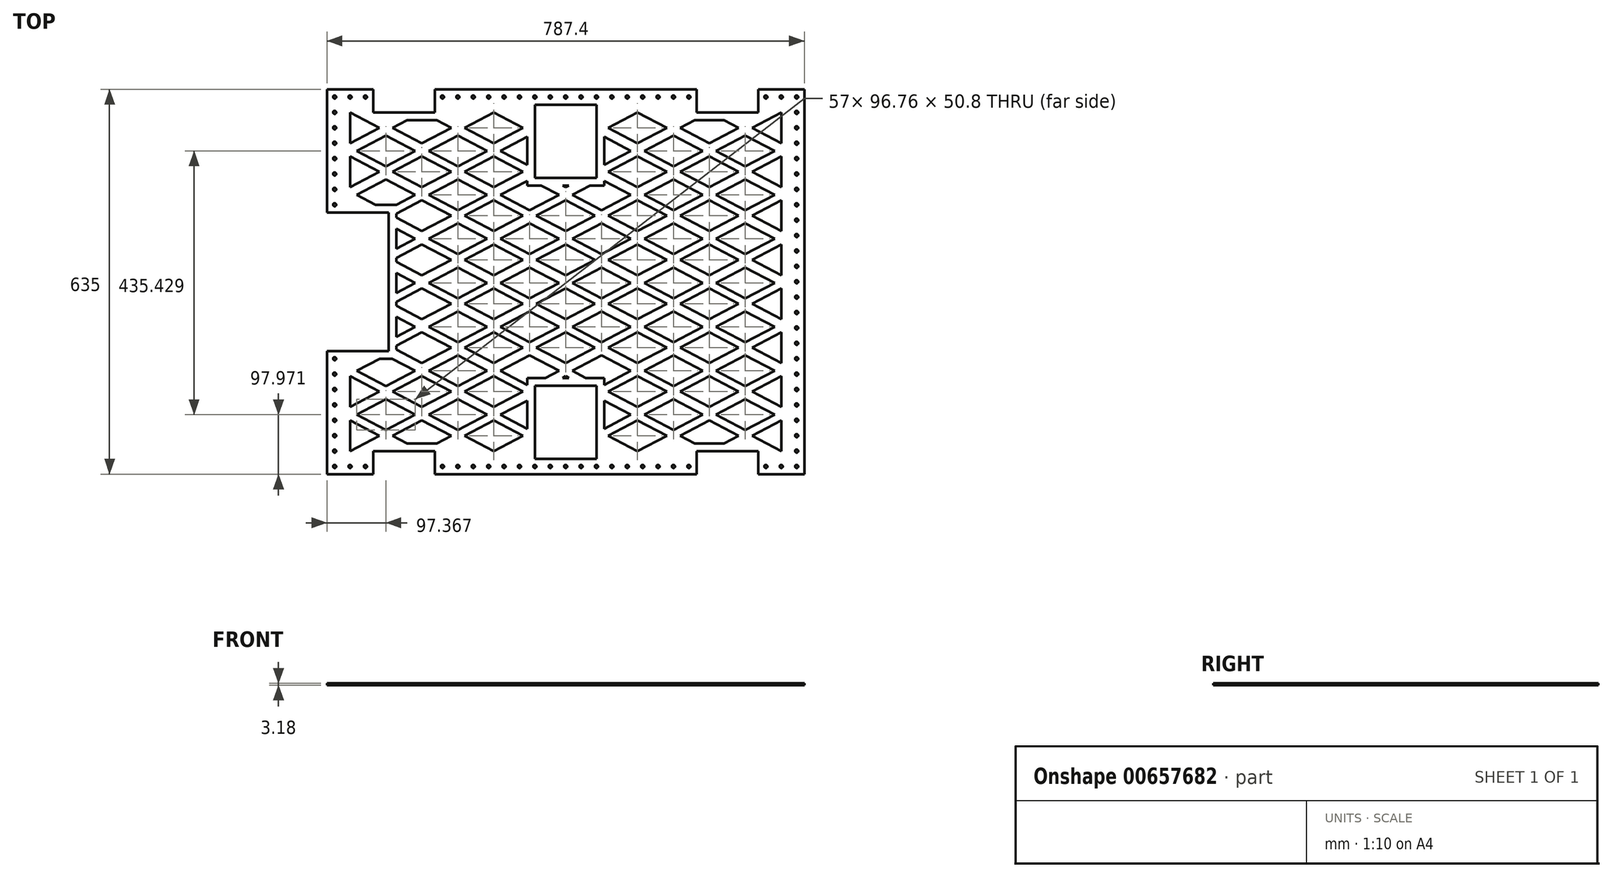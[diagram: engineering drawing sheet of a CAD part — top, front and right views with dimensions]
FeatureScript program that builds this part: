
annotation { "Feature Type Name" : "Feature", "Feature Type Description" : "" }
export const myFeature = defineFeature(function(context is Context, id is Id, definition is map)
    precondition{}
    {
        {
            var Q0;
            Q0=qCreatedBy(makeId("Top.planeOp"),FACE);
            var sketch = newSketch(context, id + "F0", { "sketchPlane" : qUnion([Q0])});
            skLineSegment(sketch, "E0.bottom", {"start": v(0, 0) * mm, "end": v(787.4, 0) * mm});
            skLineSegment(sketch, "E0.top", {"start": v(0, -635) * mm, "end": v(787.4, -635) * mm});
            skLineSegment(sketch, "E0.left", {"start": v(0, 0) * mm, "end": v(0, -635) * mm});
            skLineSegment(sketch, "E0.right", {"start": v(787.4, 0) * mm, "end": v(787.4, -635) * mm});
            skCircle(sketch, "E1", {"center": v(12.7, -622.3) * mm, "radius": 2.55 * mm});
            skCircle(sketch, "E2.0.1.0", {"center": v(12.7, -596.9) * mm, "radius": 2.55 * mm});
            skLineSegment(sketch, "E2.direction1", {"start": v(12.7, -622.3) * mm, "end": v(38.1, -622.3) * mm, "construction": true});
            skLineSegment(sketch, "E2.direction2", {"start": v(12.7, -622.3) * mm, "end": v(12.7, -596.9) * mm, "construction": true});
            skCircle(sketch, "E3.0.0.2", {"center": v(12.7, -571.5) * mm, "radius": 2.55 * mm});
            skCircle(sketch, "E4.0.0.3", {"center": v(12.7, -546.1) * mm, "radius": 2.55 * mm});
            skCircle(sketch, "E5.0.0.4", {"center": v(12.7, -520.7) * mm, "radius": 2.55 * mm});
            skCircle(sketch, "E6.0.0.5", {"center": v(12.7, -495.3) * mm, "radius": 2.55 * mm});
            skCircle(sketch, "E7.0.0.6", {"center": v(12.7, -469.9) * mm, "radius": 2.55 * mm});
            skCircle(sketch, "E8.0.0.7", {"center": v(12.7, -444.5) * mm, "radius": 2.55 * mm});
            skCircle(sketch, "E9.0.0.8", {"center": v(12.7, -419.1) * mm, "radius": 2.55 * mm});
            skCircle(sketch, "E10.0.0.9", {"center": v(12.7, -393.7) * mm, "radius": 2.55 * mm});
            skCircle(sketch, "E11.0.0.10", {"center": v(12.7, -368.3) * mm, "radius": 2.55 * mm});
            skCircle(sketch, "E12.0.0.11", {"center": v(12.7, -342.9) * mm, "radius": 2.55 * mm});
            skCircle(sketch, "E13.0.0.12", {"center": v(12.7, -317.5) * mm, "radius": 2.55 * mm});
            skCircle(sketch, "E14.0.0.13", {"center": v(12.7, -292.1) * mm, "radius": 2.55 * mm});
            skCircle(sketch, "E15.0.0.14", {"center": v(12.7, -266.7) * mm, "radius": 2.55 * mm});
            skCircle(sketch, "E16.0.0.15", {"center": v(12.7, -241.3) * mm, "radius": 2.55 * mm});
            skCircle(sketch, "E17.0.0.16", {"center": v(12.7, -215.9) * mm, "radius": 2.55 * mm});
            skCircle(sketch, "E18.0.0.17", {"center": v(12.7, -190.5) * mm, "radius": 2.55 * mm});
            skCircle(sketch, "E19.0.0.18", {"center": v(12.7, -165.1) * mm, "radius": 2.55 * mm});
            skCircle(sketch, "E20.0.0.19", {"center": v(12.7, -139.7) * mm, "radius": 2.55 * mm});
            skCircle(sketch, "E21.0.0.20", {"center": v(12.7, -114.3) * mm, "radius": 2.55 * mm});
            skCircle(sketch, "E22.0.0.21", {"center": v(12.7, -88.9) * mm, "radius": 2.55 * mm});
            skCircle(sketch, "E23.0.0.22", {"center": v(12.7, -63.5) * mm, "radius": 2.55 * mm});
            skCircle(sketch, "E24.0.0.23", {"center": v(12.7, -38.1) * mm, "radius": 2.55 * mm});
            skCircle(sketch, "E25.0.0.24", {"center": v(12.7, -12.7) * mm, "radius": 2.55 * mm});
            skCircle(sketch, "E26.1.0.0", {"center": v(38.1, -622.3) * mm, "radius": 2.55 * mm});
            skCircle(sketch, "E26.2.0.0", {"center": v(63.5, -622.3) * mm, "radius": 2.55 * mm});
            skCircle(sketch, "E26.3.0.0", {"center": v(88.9, -622.3) * mm, "radius": 2.55 * mm});
            skCircle(sketch, "E26.4.0.0", {"center": v(114.3, -622.3) * mm, "radius": 2.55 * mm});
            skCircle(sketch, "E26.5.0.0", {"center": v(139.7, -622.3) * mm, "radius": 2.55 * mm});
            skCircle(sketch, "E26.6.0.0", {"center": v(165.1, -622.3) * mm, "radius": 2.55 * mm});
            skCircle(sketch, "E26.7.0.0", {"center": v(190.5, -622.3) * mm, "radius": 2.55 * mm});
            skCircle(sketch, "E26.8.0.0", {"center": v(215.9, -622.3) * mm, "radius": 2.55 * mm});
            skCircle(sketch, "E26.9.0.0", {"center": v(241.3, -622.3) * mm, "radius": 2.55 * mm});
            skCircle(sketch, "E26.10.0.0", {"center": v(266.7, -622.3) * mm, "radius": 2.55 * mm});
            skCircle(sketch, "E26.11.0.0", {"center": v(292.1, -622.3) * mm, "radius": 2.55 * mm});
            skCircle(sketch, "E26.12.0.0", {"center": v(317.5, -622.3) * mm, "radius": 2.55 * mm});
            skCircle(sketch, "E26.13.0.0", {"center": v(342.9, -622.3) * mm, "radius": 2.55 * mm});
            skCircle(sketch, "E26.14.0.0", {"center": v(368.3, -622.3) * mm, "radius": 2.55 * mm});
            skCircle(sketch, "E26.15.0.0", {"center": v(393.7, -622.3) * mm, "radius": 2.55 * mm});
            skCircle(sketch, "E26.16.0.0", {"center": v(419.1, -622.3) * mm, "radius": 2.55 * mm});
            skCircle(sketch, "E26.17.0.0", {"center": v(444.5, -622.3) * mm, "radius": 2.55 * mm});
            skCircle(sketch, "E26.18.0.0", {"center": v(469.9, -622.3) * mm, "radius": 2.55 * mm});
            skCircle(sketch, "E26.19.0.0", {"center": v(495.3, -622.3) * mm, "radius": 2.55 * mm});
            skCircle(sketch, "E26.20.0.0", {"center": v(520.7, -622.3) * mm, "radius": 2.55 * mm});
            skCircle(sketch, "E26.21.0.0", {"center": v(546.1, -622.3) * mm, "radius": 2.55 * mm});
            skCircle(sketch, "E26.22.0.0", {"center": v(571.5, -622.3) * mm, "radius": 2.55 * mm});
            skCircle(sketch, "E26.23.0.0", {"center": v(596.9, -622.3) * mm, "radius": 2.55 * mm});
            skCircle(sketch, "E26.24.0.0", {"center": v(622.3, -622.3) * mm, "radius": 2.55 * mm});
            skCircle(sketch, "E26.25.0.0", {"center": v(647.7, -622.3) * mm, "radius": 2.55 * mm});
            skCircle(sketch, "E26.26.0.0", {"center": v(673.1, -622.3) * mm, "radius": 2.55 * mm});
            skCircle(sketch, "E26.27.0.0", {"center": v(698.5, -622.3) * mm, "radius": 2.55 * mm});
            skCircle(sketch, "E26.28.0.0", {"center": v(723.9, -622.3) * mm, "radius": 2.55 * mm});
            skCircle(sketch, "E26.29.0.0", {"center": v(749.3, -622.3) * mm, "radius": 2.55 * mm});
            skCircle(sketch, "E27.0.1.0", {"center": v(774.7, -596.9) * mm, "radius": 2.55 * mm});
            skCircle(sketch, "E27.0.2.0", {"center": v(774.7, -571.5) * mm, "radius": 2.55 * mm});
            skCircle(sketch, "E27.0.3.0", {"center": v(774.7, -546.1) * mm, "radius": 2.55 * mm});
            skCircle(sketch, "E27.0.4.0", {"center": v(774.7, -520.7) * mm, "radius": 2.55 * mm});
            skCircle(sketch, "E27.0.5.0", {"center": v(774.7, -495.3) * mm, "radius": 2.55 * mm});
            skCircle(sketch, "E27.0.6.0", {"center": v(774.7, -469.9) * mm, "radius": 2.55 * mm});
            skCircle(sketch, "E27.0.7.0", {"center": v(774.7, -444.5) * mm, "radius": 2.55 * mm});
            skCircle(sketch, "E27.0.8.0", {"center": v(774.7, -419.1) * mm, "radius": 2.55 * mm});
            skCircle(sketch, "E27.0.9.0", {"center": v(774.7, -393.7) * mm, "radius": 2.55 * mm});
            skCircle(sketch, "E27.0.10.0", {"center": v(774.7, -368.3) * mm, "radius": 2.55 * mm});
            skCircle(sketch, "E27.0.11.0", {"center": v(774.7, -342.9) * mm, "radius": 2.55 * mm});
            skCircle(sketch, "E27.0.12.0", {"center": v(774.7, -317.5) * mm, "radius": 2.55 * mm});
            skCircle(sketch, "E27.0.13.0", {"center": v(774.7, -292.1) * mm, "radius": 2.55 * mm});
            skCircle(sketch, "E27.0.14.0", {"center": v(774.7, -266.7) * mm, "radius": 2.55 * mm});
            skCircle(sketch, "E27.0.15.0", {"center": v(774.7, -241.3) * mm, "radius": 2.55 * mm});
            skCircle(sketch, "E27.0.16.0", {"center": v(774.7, -215.9) * mm, "radius": 2.55 * mm});
            skCircle(sketch, "E27.0.17.0", {"center": v(774.7, -190.5) * mm, "radius": 2.55 * mm});
            skCircle(sketch, "E27.0.18.0", {"center": v(774.7, -165.1) * mm, "radius": 2.55 * mm});
            skCircle(sketch, "E27.0.19.0", {"center": v(774.7, -139.7) * mm, "radius": 2.55 * mm});
            skCircle(sketch, "E27.0.20.0", {"center": v(774.7, -114.3) * mm, "radius": 2.55 * mm});
            skCircle(sketch, "E27.0.21.0", {"center": v(774.7, -88.9) * mm, "radius": 2.55 * mm});
            skCircle(sketch, "E27.0.22.0", {"center": v(774.7, -63.5) * mm, "radius": 2.55 * mm});
            skCircle(sketch, "E27.0.23.0", {"center": v(774.7, -38.1) * mm, "radius": 2.55 * mm});
            skCircle(sketch, "E27.0.24.0", {"center": v(774.7, -12.7) * mm, "radius": 2.55 * mm});
            skLineSegment(sketch, "E27.direction1", {"start": v(774.7, -622.3) * mm, "end": v(850.9, -622.3) * mm, "construction": true});
            skLineSegment(sketch, "E27.direction2", {"start": v(774.7, -622.3) * mm, "end": v(774.7, -596.9) * mm, "construction": true});
            skCircle(sketch, "E28.1.0.0", {"center": v(749.3, -12.7) * mm, "radius": 2.55 * mm});
            skCircle(sketch, "E28.2.0.0", {"center": v(723.9, -12.7) * mm, "radius": 2.55 * mm});
            skCircle(sketch, "E28.3.0.0", {"center": v(698.5, -12.7) * mm, "radius": 2.55 * mm});
            skCircle(sketch, "E28.4.0.0", {"center": v(673.1, -12.7) * mm, "radius": 2.55 * mm});
            skCircle(sketch, "E28.5.0.0", {"center": v(647.7, -12.7) * mm, "radius": 2.55 * mm});
            skCircle(sketch, "E28.6.0.0", {"center": v(622.3, -12.7) * mm, "radius": 2.55 * mm});
            skCircle(sketch, "E28.7.0.0", {"center": v(596.9, -12.7) * mm, "radius": 2.55 * mm});
            skCircle(sketch, "E28.8.0.0", {"center": v(571.5, -12.7) * mm, "radius": 2.55 * mm});
            skCircle(sketch, "E28.9.0.0", {"center": v(546.1, -12.7) * mm, "radius": 2.55 * mm});
            skCircle(sketch, "E28.10.0.0", {"center": v(520.7, -12.7) * mm, "radius": 2.55 * mm});
            skCircle(sketch, "E28.11.0.0", {"center": v(495.3, -12.7) * mm, "radius": 2.55 * mm});
            skCircle(sketch, "E28.12.0.0", {"center": v(469.9, -12.7) * mm, "radius": 2.55 * mm});
            skCircle(sketch, "E28.13.0.0", {"center": v(444.5, -12.7) * mm, "radius": 2.55 * mm});
            skCircle(sketch, "E28.14.0.0", {"center": v(419.1, -12.7) * mm, "radius": 2.55 * mm});
            skCircle(sketch, "E28.15.0.0", {"center": v(393.7, -12.7) * mm, "radius": 2.55 * mm});
            skCircle(sketch, "E28.16.0.0", {"center": v(368.3, -12.7) * mm, "radius": 2.55 * mm});
            skCircle(sketch, "E28.17.0.0", {"center": v(342.9, -12.7) * mm, "radius": 2.55 * mm});
            skCircle(sketch, "E28.18.0.0", {"center": v(317.5, -12.7) * mm, "radius": 2.55 * mm});
            skCircle(sketch, "E28.19.0.0", {"center": v(292.1, -12.7) * mm, "radius": 2.55 * mm});
            skCircle(sketch, "E28.20.0.0", {"center": v(266.7, -12.7) * mm, "radius": 2.55 * mm});
            skCircle(sketch, "E28.21.0.0", {"center": v(241.3, -12.7) * mm, "radius": 2.55 * mm});
            skCircle(sketch, "E28.22.0.0", {"center": v(215.9, -12.7) * mm, "radius": 2.55 * mm});
            skCircle(sketch, "E28.23.0.0", {"center": v(190.5, -12.7) * mm, "radius": 2.55 * mm});
            skCircle(sketch, "E28.24.0.0", {"center": v(165.1, -12.7) * mm, "radius": 2.55 * mm});
            skCircle(sketch, "E28.25.0.0", {"center": v(139.7, -12.7) * mm, "radius": 2.55 * mm});
            skCircle(sketch, "E28.26.0.0", {"center": v(114.3, -12.7) * mm, "radius": 2.55 * mm});
            skCircle(sketch, "E28.27.0.0", {"center": v(88.9, -12.7) * mm, "radius": 2.55 * mm});
            skCircle(sketch, "E28.28.0.0", {"center": v(63.5, -12.7) * mm, "radius": 2.55 * mm});
            skCircle(sketch, "E28.29.0.0", {"center": v(38.1, -12.7) * mm, "radius": 2.55 * mm});
            skCircle(sketch, "E28.31.0.0", {"center": v(-12.7, -12.7) * mm, "radius": 2.55 * mm});
            skLineSegment(sketch, "E28.direction1", {"start": v(774.7, -12.7) * mm, "end": v(749.3, -12.7) * mm, "construction": true});
            skLineSegment(sketch, "E29.bottom", {"start": v(444.5, -609.6) * mm, "end": v(342.9, -609.6) * mm});
            skLineSegment(sketch, "E29.top", {"start": v(444.5, -488.95) * mm, "end": v(342.9, -488.95) * mm});
            skLineSegment(sketch, "E29.left", {"start": v(444.5, -609.6) * mm, "end": v(444.5, -488.95) * mm});
            skLineSegment(sketch, "E29.right", {"start": v(342.9, -609.6) * mm, "end": v(342.9, -488.95) * mm});
            skLineSegment(sketch, "E30.bottom", {"start": v(342.9, -25.4) * mm, "end": v(444.5, -25.4) * mm});
            skLineSegment(sketch, "E30.top", {"start": v(342.9, -146.05) * mm, "end": v(444.5, -146.05) * mm});
            skLineSegment(sketch, "E30.left", {"start": v(342.9, -25.4) * mm, "end": v(342.9, -146.05) * mm});
            skLineSegment(sketch, "E30.right", {"start": v(444.5, -25.4) * mm, "end": v(444.5, -146.05) * mm});
            skLineSegment(sketch, "E31.bottom", {"start": v(0, -203.2) * mm, "end": v(101.6, -203.2) * mm});
            skLineSegment(sketch, "E31.top", {"start": v(0, -431.8) * mm, "end": v(101.6, -431.8) * mm});
            skLineSegment(sketch, "E31.left", {"start": v(0, -203.2) * mm, "end": v(0, -431.8) * mm});
            skLineSegment(sketch, "E31.right", {"start": v(101.6, -203.2) * mm, "end": v(101.6, -431.8) * mm});
            skLineSegment(sketch, "E32.left", {"start": v(787.4, -533.4) * mm, "end": v(787.4, -101.6) * mm});
            skLineSegment(sketch, "E33", {"start": v(342.9, -609.6) * mm, "end": v(342.9, -609.6) * mm});
            skLineSegment(sketch, "E34", {"start": v(444.5, -609.6) * mm, "end": v(444.5, -609.6) * mm});
            skCircle(sketch, "E35.0.30.0", {"center": v(774.7, -622.3) * mm, "radius": 2.55 * mm});
            skLineSegment(sketch, "E36.bottom", {"start": v(76.2, -635) * mm, "end": v(177.8, -635) * mm});
            skLineSegment(sketch, "E36.top", {"start": v(76.2, -596.9) * mm, "end": v(177.8, -596.9) * mm});
            skLineSegment(sketch, "E36.left", {"start": v(76.2, -635) * mm, "end": v(76.2, -596.9) * mm});
            skLineSegment(sketch, "E36.right", {"start": v(177.8, -635) * mm, "end": v(177.8, -596.9) * mm});
            skLineSegment(sketch, "E37.bottom", {"start": v(711.2, -635) * mm, "end": v(609.6, -635) * mm});
            skLineSegment(sketch, "E37.top", {"start": v(711.2, -596.9) * mm, "end": v(609.6, -596.9) * mm});
            skLineSegment(sketch, "E37.left", {"start": v(711.2, -635) * mm, "end": v(711.2, -596.9) * mm});
            skLineSegment(sketch, "E37.right", {"start": v(609.6, -635) * mm, "end": v(609.6, -596.9) * mm});
            skLineSegment(sketch, "E38.bottom", {"start": v(711.2, 0) * mm, "end": v(609.6, 0) * mm});
            skLineSegment(sketch, "E38.top", {"start": v(711.2, -38.1) * mm, "end": v(609.6, -38.1) * mm});
            skLineSegment(sketch, "E38.left", {"start": v(711.2, 0) * mm, "end": v(711.2, -38.1) * mm});
            skLineSegment(sketch, "E38.right", {"start": v(609.6, 0) * mm, "end": v(609.6, -38.1) * mm});
            skLineSegment(sketch, "E39.bottom", {"start": v(76.2, 0) * mm, "end": v(177.8, 0) * mm});
            skLineSegment(sketch, "E39.top", {"start": v(76.2, -38.1) * mm, "end": v(177.8, -38.1) * mm});
            skLineSegment(sketch, "E39.left", {"start": v(76.2, 0) * mm, "end": v(76.2, -38.1) * mm});
            skLineSegment(sketch, "E39.right", {"start": v(177.8, 0) * mm, "end": v(177.8, -38.1) * mm});
            skLineSegment(sketch, "E40", {"start": v(38.1, -38.1) * mm, "end": v(38.1, -88.9) * mm});
            skLineSegment(sketch, "E41", {"start": v(38.1, -88.9) * mm, "end": v(86.48, -63.5) * mm});
            skLineSegment(sketch, "E42", {"start": v(86.48, -63.5) * mm, "end": v(38.1, -38.1) * mm});
            skLineSegment(sketch, "E43", {"start": v(97.37, -127) * mm, "end": v(48.99, -101.6) * mm});
            skLineSegment(sketch, "E44", {"start": v(48.99, -101.6) * mm, "end": v(97.37, -76.2) * mm});
            skLineSegment(sketch, "E45", {"start": v(97.37, -76.2) * mm, "end": v(97.37, -127) * mm, "construction": true});
            skLineSegment(sketch, "E46", {"start": v(97.37, -127) * mm, "end": v(145.75, -101.6) * mm});
            skLineSegment(sketch, "E47", {"start": v(145.75, -101.6) * mm, "end": v(97.37, -76.2) * mm});
            skLineSegment(sketch, "E48", {"start": v(156.63, -88.9) * mm, "end": v(108.25, -63.5) * mm});
            skLineSegment(sketch, "E49", {"start": v(108.25, -63.5) * mm, "end": v(156.63, -38.1) * mm});
            skLineSegment(sketch, "E50", {"start": v(156.63, -38.1) * mm, "end": v(205.01, -63.5) * mm});
            skLineSegment(sketch, "E51", {"start": v(205.01, -63.5) * mm, "end": v(156.63, -88.9) * mm});
            skLineSegment(sketch, "E52", {"start": v(156.63, -88.9) * mm, "end": v(156.63, -38.1) * mm});
            skLineSegment(sketch, "E53.0.1.0", {"start": v(38.1, -161.47) * mm, "end": v(86.48, -136.07) * mm});
            skLineSegment(sketch, "E53.0.1.1", {"start": v(38.1, -110.67) * mm, "end": v(38.1, -161.47) * mm});
            skLineSegment(sketch, "E53.0.1.2", {"start": v(86.48, -136.07) * mm, "end": v(38.1, -110.67) * mm});
            skLineSegment(sketch, "E53.0.2.0", {"start": v(38.1, -234.04) * mm, "end": v(86.48, -208.64) * mm, "construction": true});
            skLineSegment(sketch, "E53.0.2.1", {"start": v(38.1, -183.24) * mm, "end": v(38.1, -234.04) * mm, "construction": true});
            skLineSegment(sketch, "E53.0.2.2", {"start": v(86.48, -208.64) * mm, "end": v(38.1, -183.24) * mm, "construction": true});
            skLineSegment(sketch, "E53.0.3.0", {"start": v(38.1, -306.61) * mm, "end": v(86.48, -281.21) * mm, "construction": true});
            skLineSegment(sketch, "E53.0.3.1", {"start": v(38.1, -255.81) * mm, "end": v(38.1, -306.61) * mm, "construction": true});
            skLineSegment(sketch, "E53.0.3.2", {"start": v(86.48, -281.21) * mm, "end": v(38.1, -255.81) * mm, "construction": true});
            skLineSegment(sketch, "E53.0.4.0", {"start": v(38.1, -379.19) * mm, "end": v(86.48, -353.79) * mm, "construction": true});
            skLineSegment(sketch, "E53.0.4.1", {"start": v(38.1, -328.39) * mm, "end": v(38.1, -379.19) * mm, "construction": true});
            skLineSegment(sketch, "E53.0.4.2", {"start": v(86.48, -353.79) * mm, "end": v(38.1, -328.39) * mm, "construction": true});
            skLineSegment(sketch, "E53.0.5.0", {"start": v(38.1, -451.76) * mm, "end": v(86.48, -426.36) * mm, "construction": true});
            skLineSegment(sketch, "E53.0.5.1", {"start": v(38.1, -400.96) * mm, "end": v(38.1, -451.76) * mm, "construction": true});
            skLineSegment(sketch, "E53.0.5.2", {"start": v(86.48, -426.36) * mm, "end": v(38.1, -400.96) * mm, "construction": true});
            skLineSegment(sketch, "E53.0.6.0", {"start": v(38.1, -524.33) * mm, "end": v(86.48, -498.93) * mm});
            skLineSegment(sketch, "E53.0.6.1", {"start": v(38.1, -473.53) * mm, "end": v(38.1, -524.33) * mm});
            skLineSegment(sketch, "E53.0.6.2", {"start": v(86.48, -498.93) * mm, "end": v(38.1, -473.53) * mm});
            skLineSegment(sketch, "E53.0.7.0", {"start": v(38.1, -596.9) * mm, "end": v(86.48, -571.5) * mm});
            skLineSegment(sketch, "E53.0.7.1", {"start": v(38.1, -546.1) * mm, "end": v(38.1, -596.9) * mm});
            skLineSegment(sketch, "E53.0.7.2", {"start": v(86.48, -571.5) * mm, "end": v(38.1, -546.1) * mm});
            skLineSegment(sketch, "E53.direction1", {"start": v(38.1, -88.9) * mm, "end": v(63.5, -88.9) * mm, "construction": true});
            skLineSegment(sketch, "E53.direction2", {"start": v(38.1, -88.9) * mm, "end": v(38.1, -161.47) * mm, "construction": true});
            skLineSegment(sketch, "E54.0.1.0", {"start": v(108.25, -136.07) * mm, "end": v(156.63, -110.67) * mm});
            skLineSegment(sketch, "E54.0.1.1", {"start": v(156.63, -110.67) * mm, "end": v(205.01, -136.07) * mm});
            skLineSegment(sketch, "E54.0.1.2", {"start": v(205.01, -136.07) * mm, "end": v(156.63, -161.47) * mm});
            skLineSegment(sketch, "E54.0.1.3", {"start": v(156.63, -161.47) * mm, "end": v(108.25, -136.07) * mm});
            skLineSegment(sketch, "E54.1.0.0", {"start": v(226.79, -63.5) * mm, "end": v(275.17, -38.1) * mm});
            skLineSegment(sketch, "E54.1.0.1", {"start": v(275.17, -38.1) * mm, "end": v(323.55, -63.5) * mm});
            skLineSegment(sketch, "E54.1.0.2", {"start": v(323.55, -63.5) * mm, "end": v(275.17, -88.9) * mm});
            skLineSegment(sketch, "E54.1.0.3", {"start": v(275.17, -88.9) * mm, "end": v(226.79, -63.5) * mm});
            skLineSegment(sketch, "E54.1.1.0", {"start": v(226.79, -136.07) * mm, "end": v(275.17, -110.67) * mm});
            skLineSegment(sketch, "E54.1.1.1", {"start": v(275.17, -110.67) * mm, "end": v(323.55, -136.07) * mm});
            skLineSegment(sketch, "E54.1.1.2", {"start": v(323.55, -136.07) * mm, "end": v(275.17, -161.47) * mm});
            skLineSegment(sketch, "E54.1.1.3", {"start": v(275.17, -161.47) * mm, "end": v(226.79, -136.07) * mm});
            skLineSegment(sketch, "E54.2.0.0", {"start": v(345.32, -63.5) * mm, "end": v(393.7, -38.1) * mm, "construction": true});
            skLineSegment(sketch, "E54.2.0.1", {"start": v(393.7, -38.1) * mm, "end": v(442.08, -63.5) * mm, "construction": true});
            skLineSegment(sketch, "E54.2.0.2", {"start": v(442.08, -63.5) * mm, "end": v(393.7, -88.9) * mm, "construction": true});
            skLineSegment(sketch, "E54.2.0.3", {"start": v(393.7, -88.9) * mm, "end": v(345.32, -63.5) * mm, "construction": true});
            skLineSegment(sketch, "E54.2.1.0", {"start": v(345.32, -136.07) * mm, "end": v(393.7, -110.67) * mm, "construction": true});
            skLineSegment(sketch, "E54.2.1.1", {"start": v(393.7, -110.67) * mm, "end": v(442.08, -136.07) * mm, "construction": true});
            skLineSegment(sketch, "E54.2.1.2", {"start": v(442.08, -136.07) * mm, "end": v(393.7, -161.47) * mm});
            skLineSegment(sketch, "E54.2.1.3", {"start": v(393.7, -161.47) * mm, "end": v(345.32, -136.07) * mm});
            skLineSegment(sketch, "E54.direction1", {"start": v(108.25, -63.5) * mm, "end": v(226.79, -63.5) * mm, "construction": true});
            skLineSegment(sketch, "E54.direction2", {"start": v(108.25, -63.5) * mm, "end": v(108.25, -136.07) * mm, "construction": true});
            skLineSegment(sketch, "E55.0.3.0", {"start": v(463.85, -63.5) * mm, "end": v(512.23, -38.1) * mm});
            skLineSegment(sketch, "E55.3.3.0", {"start": v(512.23, -38.1) * mm, "end": v(560.61, -63.5) * mm});
            skLineSegment(sketch, "E55.6.3.0", {"start": v(560.61, -63.5) * mm, "end": v(512.23, -88.9) * mm});
            skLineSegment(sketch, "E55.9.3.0", {"start": v(512.23, -88.9) * mm, "end": v(463.85, -63.5) * mm});
            skLineSegment(sketch, "E55.0.3.1", {"start": v(463.85, -136.07) * mm, "end": v(512.23, -110.67) * mm});
            skLineSegment(sketch, "E55.3.3.1", {"start": v(512.23, -110.67) * mm, "end": v(560.61, -136.07) * mm});
            skLineSegment(sketch, "E55.6.3.1", {"start": v(560.61, -136.07) * mm, "end": v(512.23, -161.47) * mm});
            skLineSegment(sketch, "E55.9.3.1", {"start": v(512.23, -161.47) * mm, "end": v(463.85, -136.07) * mm});
            skLineSegment(sketch, "E55.0.4.0", {"start": v(582.39, -63.5) * mm, "end": v(630.77, -38.1) * mm});
            skLineSegment(sketch, "E55.3.4.0", {"start": v(630.77, -38.1) * mm, "end": v(679.15, -63.5) * mm});
            skLineSegment(sketch, "E55.6.4.0", {"start": v(679.15, -63.5) * mm, "end": v(630.77, -88.9) * mm});
            skLineSegment(sketch, "E55.9.4.0", {"start": v(630.77, -88.9) * mm, "end": v(582.39, -63.5) * mm});
            skLineSegment(sketch, "E55.0.4.1", {"start": v(582.39, -136.07) * mm, "end": v(630.77, -110.67) * mm});
            skLineSegment(sketch, "E55.3.4.1", {"start": v(630.77, -110.67) * mm, "end": v(679.15, -136.07) * mm});
            skLineSegment(sketch, "E55.6.4.1", {"start": v(679.15, -136.07) * mm, "end": v(630.77, -161.47) * mm});
            skLineSegment(sketch, "E55.9.4.1", {"start": v(630.77, -161.47) * mm, "end": v(582.39, -136.07) * mm});
            skLineSegment(sketch, "E56.0.0.2", {"start": v(108.25, -208.64) * mm, "end": v(156.63, -183.24) * mm});
            skLineSegment(sketch, "E56.3.0.2", {"start": v(156.63, -183.24) * mm, "end": v(205.01, -208.64) * mm});
            skLineSegment(sketch, "E56.6.0.2", {"start": v(205.01, -208.64) * mm, "end": v(156.63, -234.04) * mm});
            skLineSegment(sketch, "E56.9.0.2", {"start": v(156.63, -234.04) * mm, "end": v(108.25, -208.64) * mm});
            skLineSegment(sketch, "E56.0.0.3", {"start": v(108.25, -281.21) * mm, "end": v(156.63, -255.81) * mm});
            skLineSegment(sketch, "E56.3.0.3", {"start": v(156.63, -255.81) * mm, "end": v(205.01, -281.21) * mm});
            skLineSegment(sketch, "E56.6.0.3", {"start": v(205.01, -281.21) * mm, "end": v(156.63, -306.61) * mm});
            skLineSegment(sketch, "E56.9.0.3", {"start": v(156.63, -306.61) * mm, "end": v(108.25, -281.21) * mm});
            skLineSegment(sketch, "E56.0.0.4", {"start": v(108.25, -353.79) * mm, "end": v(156.63, -328.39) * mm});
            skLineSegment(sketch, "E56.3.0.4", {"start": v(156.63, -328.39) * mm, "end": v(205.01, -353.79) * mm});
            skLineSegment(sketch, "E56.6.0.4", {"start": v(205.01, -353.79) * mm, "end": v(156.63, -379.19) * mm});
            skLineSegment(sketch, "E56.9.0.4", {"start": v(156.63, -379.19) * mm, "end": v(108.25, -353.79) * mm});
            skLineSegment(sketch, "E56.0.0.5", {"start": v(108.25, -426.36) * mm, "end": v(156.63, -400.96) * mm});
            skLineSegment(sketch, "E56.3.0.5", {"start": v(156.63, -400.96) * mm, "end": v(205.01, -426.36) * mm});
            skLineSegment(sketch, "E56.6.0.5", {"start": v(205.01, -426.36) * mm, "end": v(156.63, -451.76) * mm});
            skLineSegment(sketch, "E56.9.0.5", {"start": v(156.63, -451.76) * mm, "end": v(108.25, -426.36) * mm});
            skLineSegment(sketch, "E56.0.0.6", {"start": v(108.25, -498.93) * mm, "end": v(156.63, -473.53) * mm});
            skLineSegment(sketch, "E56.3.0.6", {"start": v(156.63, -473.53) * mm, "end": v(205.01, -498.93) * mm});
            skLineSegment(sketch, "E56.6.0.6", {"start": v(205.01, -498.93) * mm, "end": v(156.63, -524.33) * mm});
            skLineSegment(sketch, "E56.9.0.6", {"start": v(156.63, -524.33) * mm, "end": v(108.25, -498.93) * mm});
            skLineSegment(sketch, "E56.0.0.7", {"start": v(108.25, -571.5) * mm, "end": v(156.63, -546.1) * mm});
            skLineSegment(sketch, "E56.3.0.7", {"start": v(156.63, -546.1) * mm, "end": v(205.01, -571.5) * mm});
            skLineSegment(sketch, "E56.6.0.7", {"start": v(205.01, -571.5) * mm, "end": v(156.63, -596.9) * mm});
            skLineSegment(sketch, "E56.9.0.7", {"start": v(156.63, -596.9) * mm, "end": v(108.25, -571.5) * mm});
            skLineSegment(sketch, "E56.0.1.2", {"start": v(226.79, -208.64) * mm, "end": v(275.17, -183.24) * mm});
            skLineSegment(sketch, "E56.3.1.2", {"start": v(275.17, -183.24) * mm, "end": v(323.55, -208.64) * mm});
            skLineSegment(sketch, "E56.6.1.2", {"start": v(323.55, -208.64) * mm, "end": v(275.17, -234.04) * mm});
            skLineSegment(sketch, "E56.9.1.2", {"start": v(275.17, -234.04) * mm, "end": v(226.79, -208.64) * mm});
            skLineSegment(sketch, "E56.0.1.3", {"start": v(226.79, -281.21) * mm, "end": v(275.17, -255.81) * mm});
            skLineSegment(sketch, "E56.3.1.3", {"start": v(275.17, -255.81) * mm, "end": v(323.55, -281.21) * mm});
            skLineSegment(sketch, "E56.6.1.3", {"start": v(323.55, -281.21) * mm, "end": v(275.17, -306.61) * mm});
            skLineSegment(sketch, "E56.9.1.3", {"start": v(275.17, -306.61) * mm, "end": v(226.79, -281.21) * mm});
            skLineSegment(sketch, "E56.0.1.4", {"start": v(226.79, -353.79) * mm, "end": v(275.17, -328.39) * mm});
            skLineSegment(sketch, "E56.3.1.4", {"start": v(275.17, -328.39) * mm, "end": v(323.55, -353.79) * mm});
            skLineSegment(sketch, "E56.6.1.4", {"start": v(323.55, -353.79) * mm, "end": v(275.17, -379.19) * mm});
            skLineSegment(sketch, "E56.9.1.4", {"start": v(275.17, -379.19) * mm, "end": v(226.79, -353.79) * mm});
            skLineSegment(sketch, "E56.0.1.5", {"start": v(226.79, -426.36) * mm, "end": v(275.17, -400.96) * mm});
            skLineSegment(sketch, "E56.3.1.5", {"start": v(275.17, -400.96) * mm, "end": v(323.55, -426.36) * mm});
            skLineSegment(sketch, "E56.6.1.5", {"start": v(323.55, -426.36) * mm, "end": v(275.17, -451.76) * mm});
            skLineSegment(sketch, "E56.9.1.5", {"start": v(275.17, -451.76) * mm, "end": v(226.79, -426.36) * mm});
            skLineSegment(sketch, "E56.0.1.6", {"start": v(226.79, -498.93) * mm, "end": v(275.17, -473.53) * mm});
            skLineSegment(sketch, "E56.3.1.6", {"start": v(275.17, -473.53) * mm, "end": v(323.55, -498.93) * mm});
            skLineSegment(sketch, "E56.6.1.6", {"start": v(323.55, -498.93) * mm, "end": v(275.17, -524.33) * mm});
            skLineSegment(sketch, "E56.9.1.6", {"start": v(275.17, -524.33) * mm, "end": v(226.79, -498.93) * mm});
            skLineSegment(sketch, "E56.0.1.7", {"start": v(226.79, -571.5) * mm, "end": v(275.17, -546.1) * mm});
            skLineSegment(sketch, "E56.3.1.7", {"start": v(275.17, -546.1) * mm, "end": v(323.55, -571.5) * mm});
            skLineSegment(sketch, "E56.6.1.7", {"start": v(323.55, -571.5) * mm, "end": v(275.17, -596.9) * mm});
            skLineSegment(sketch, "E56.9.1.7", {"start": v(275.17, -596.9) * mm, "end": v(226.79, -571.5) * mm});
            skLineSegment(sketch, "E56.0.2.2", {"start": v(345.32, -208.64) * mm, "end": v(393.7, -183.24) * mm});
            skLineSegment(sketch, "E56.3.2.2", {"start": v(393.7, -183.24) * mm, "end": v(442.08, -208.64) * mm});
            skLineSegment(sketch, "E56.6.2.2", {"start": v(442.08, -208.64) * mm, "end": v(393.7, -234.04) * mm});
            skLineSegment(sketch, "E56.9.2.2", {"start": v(393.7, -234.04) * mm, "end": v(345.32, -208.64) * mm});
            skLineSegment(sketch, "E56.0.2.3", {"start": v(345.32, -281.21) * mm, "end": v(393.7, -255.81) * mm});
            skLineSegment(sketch, "E56.3.2.3", {"start": v(393.7, -255.81) * mm, "end": v(442.08, -281.21) * mm});
            skLineSegment(sketch, "E56.6.2.3", {"start": v(442.08, -281.21) * mm, "end": v(393.7, -306.61) * mm});
            skLineSegment(sketch, "E56.9.2.3", {"start": v(393.7, -306.61) * mm, "end": v(345.32, -281.21) * mm});
            skLineSegment(sketch, "E56.0.2.4", {"start": v(345.32, -353.79) * mm, "end": v(393.7, -328.39) * mm});
            skLineSegment(sketch, "E56.3.2.4", {"start": v(393.7, -328.39) * mm, "end": v(442.08, -353.79) * mm});
            skLineSegment(sketch, "E56.6.2.4", {"start": v(442.08, -353.79) * mm, "end": v(393.7, -379.19) * mm});
            skLineSegment(sketch, "E56.9.2.4", {"start": v(393.7, -379.19) * mm, "end": v(345.32, -353.79) * mm});
            skLineSegment(sketch, "E56.0.2.5", {"start": v(345.32, -426.36) * mm, "end": v(393.7, -400.96) * mm});
            skLineSegment(sketch, "E56.3.2.5", {"start": v(393.7, -400.96) * mm, "end": v(442.08, -426.36) * mm});
            skLineSegment(sketch, "E56.6.2.5", {"start": v(442.08, -426.36) * mm, "end": v(393.7, -451.76) * mm});
            skLineSegment(sketch, "E56.9.2.5", {"start": v(393.7, -451.76) * mm, "end": v(345.32, -426.36) * mm});
            skLineSegment(sketch, "E56.0.2.6", {"start": v(345.32, -498.93) * mm, "end": v(393.7, -473.53) * mm});
            skLineSegment(sketch, "E56.3.2.6", {"start": v(393.7, -473.53) * mm, "end": v(442.08, -498.93) * mm});
            skLineSegment(sketch, "E56.6.2.6", {"start": v(442.08, -498.93) * mm, "end": v(393.7, -524.33) * mm});
            skLineSegment(sketch, "E56.9.2.6", {"start": v(393.7, -524.33) * mm, "end": v(345.32, -498.93) * mm});
            skLineSegment(sketch, "E56.0.2.7", {"start": v(345.32, -571.5) * mm, "end": v(393.7, -546.1) * mm});
            skLineSegment(sketch, "E56.3.2.7", {"start": v(393.7, -546.1) * mm, "end": v(442.08, -571.5) * mm});
            skLineSegment(sketch, "E56.6.2.7", {"start": v(442.08, -571.5) * mm, "end": v(393.7, -596.9) * mm});
            skLineSegment(sketch, "E56.9.2.7", {"start": v(393.7, -596.9) * mm, "end": v(345.32, -571.5) * mm});
            skLineSegment(sketch, "E56.0.3.2", {"start": v(463.85, -208.64) * mm, "end": v(512.23, -183.24) * mm});
            skLineSegment(sketch, "E56.3.3.2", {"start": v(512.23, -183.24) * mm, "end": v(560.61, -208.64) * mm});
            skLineSegment(sketch, "E56.6.3.2", {"start": v(560.61, -208.64) * mm, "end": v(512.23, -234.04) * mm});
            skLineSegment(sketch, "E56.9.3.2", {"start": v(512.23, -234.04) * mm, "end": v(463.85, -208.64) * mm});
            skLineSegment(sketch, "E56.0.3.3", {"start": v(463.85, -281.21) * mm, "end": v(512.23, -255.81) * mm});
            skLineSegment(sketch, "E56.3.3.3", {"start": v(512.23, -255.81) * mm, "end": v(560.61, -281.21) * mm});
            skLineSegment(sketch, "E56.6.3.3", {"start": v(560.61, -281.21) * mm, "end": v(512.23, -306.61) * mm});
            skLineSegment(sketch, "E56.9.3.3", {"start": v(512.23, -306.61) * mm, "end": v(463.85, -281.21) * mm});
            skLineSegment(sketch, "E56.0.3.4", {"start": v(463.85, -353.79) * mm, "end": v(512.23, -328.39) * mm});
            skLineSegment(sketch, "E56.3.3.4", {"start": v(512.23, -328.39) * mm, "end": v(560.61, -353.79) * mm});
            skLineSegment(sketch, "E56.6.3.4", {"start": v(560.61, -353.79) * mm, "end": v(512.23, -379.19) * mm});
            skLineSegment(sketch, "E56.9.3.4", {"start": v(512.23, -379.19) * mm, "end": v(463.85, -353.79) * mm});
            skLineSegment(sketch, "E56.0.3.5", {"start": v(463.85, -426.36) * mm, "end": v(512.23, -400.96) * mm});
            skLineSegment(sketch, "E56.3.3.5", {"start": v(512.23, -400.96) * mm, "end": v(560.61, -426.36) * mm});
            skLineSegment(sketch, "E56.6.3.5", {"start": v(560.61, -426.36) * mm, "end": v(512.23, -451.76) * mm});
            skLineSegment(sketch, "E56.9.3.5", {"start": v(512.23, -451.76) * mm, "end": v(463.85, -426.36) * mm});
            skLineSegment(sketch, "E56.0.3.6", {"start": v(463.85, -498.93) * mm, "end": v(512.23, -473.53) * mm});
            skLineSegment(sketch, "E56.3.3.6", {"start": v(512.23, -473.53) * mm, "end": v(560.61, -498.93) * mm});
            skLineSegment(sketch, "E56.6.3.6", {"start": v(560.61, -498.93) * mm, "end": v(512.23, -524.33) * mm});
            skLineSegment(sketch, "E56.9.3.6", {"start": v(512.23, -524.33) * mm, "end": v(463.85, -498.93) * mm});
            skLineSegment(sketch, "E56.0.3.7", {"start": v(463.85, -571.5) * mm, "end": v(512.23, -546.1) * mm});
            skLineSegment(sketch, "E56.3.3.7", {"start": v(512.23, -546.1) * mm, "end": v(560.61, -571.5) * mm});
            skLineSegment(sketch, "E56.6.3.7", {"start": v(560.61, -571.5) * mm, "end": v(512.23, -596.9) * mm});
            skLineSegment(sketch, "E56.9.3.7", {"start": v(512.23, -596.9) * mm, "end": v(463.85, -571.5) * mm});
            skLineSegment(sketch, "E56.0.4.2", {"start": v(582.39, -208.64) * mm, "end": v(630.77, -183.24) * mm});
            skLineSegment(sketch, "E56.3.4.2", {"start": v(630.77, -183.24) * mm, "end": v(679.15, -208.64) * mm});
            skLineSegment(sketch, "E56.6.4.2", {"start": v(679.15, -208.64) * mm, "end": v(630.77, -234.04) * mm});
            skLineSegment(sketch, "E56.9.4.2", {"start": v(630.77, -234.04) * mm, "end": v(582.39, -208.64) * mm});
            skLineSegment(sketch, "E56.0.4.3", {"start": v(582.39, -281.21) * mm, "end": v(630.77, -255.81) * mm});
            skLineSegment(sketch, "E56.3.4.3", {"start": v(630.77, -255.81) * mm, "end": v(679.15, -281.21) * mm});
            skLineSegment(sketch, "E56.6.4.3", {"start": v(679.15, -281.21) * mm, "end": v(630.77, -306.61) * mm});
            skLineSegment(sketch, "E56.9.4.3", {"start": v(630.77, -306.61) * mm, "end": v(582.39, -281.21) * mm});
            skLineSegment(sketch, "E56.0.4.4", {"start": v(582.39, -353.79) * mm, "end": v(630.77, -328.39) * mm});
            skLineSegment(sketch, "E56.3.4.4", {"start": v(630.77, -328.39) * mm, "end": v(679.15, -353.79) * mm});
            skLineSegment(sketch, "E56.6.4.4", {"start": v(679.15, -353.79) * mm, "end": v(630.77, -379.19) * mm});
            skLineSegment(sketch, "E56.9.4.4", {"start": v(630.77, -379.19) * mm, "end": v(582.39, -353.79) * mm});
            skLineSegment(sketch, "E56.0.4.5", {"start": v(582.39, -426.36) * mm, "end": v(630.77, -400.96) * mm});
            skLineSegment(sketch, "E56.3.4.5", {"start": v(630.77, -400.96) * mm, "end": v(679.15, -426.36) * mm});
            skLineSegment(sketch, "E56.6.4.5", {"start": v(679.15, -426.36) * mm, "end": v(630.77, -451.76) * mm});
            skLineSegment(sketch, "E56.9.4.5", {"start": v(630.77, -451.76) * mm, "end": v(582.39, -426.36) * mm});
            skLineSegment(sketch, "E56.0.4.6", {"start": v(582.39, -498.93) * mm, "end": v(630.77, -473.53) * mm});
            skLineSegment(sketch, "E56.3.4.6", {"start": v(630.77, -473.53) * mm, "end": v(679.15, -498.93) * mm});
            skLineSegment(sketch, "E56.6.4.6", {"start": v(679.15, -498.93) * mm, "end": v(630.77, -524.33) * mm});
            skLineSegment(sketch, "E56.9.4.6", {"start": v(630.77, -524.33) * mm, "end": v(582.39, -498.93) * mm});
            skLineSegment(sketch, "E56.0.4.7", {"start": v(582.39, -571.5) * mm, "end": v(630.77, -546.1) * mm});
            skLineSegment(sketch, "E56.3.4.7", {"start": v(630.77, -546.1) * mm, "end": v(679.15, -571.5) * mm});
            skLineSegment(sketch, "E56.6.4.7", {"start": v(679.15, -571.5) * mm, "end": v(630.77, -596.9) * mm});
            skLineSegment(sketch, "E56.9.4.7", {"start": v(630.77, -596.9) * mm, "end": v(582.39, -571.5) * mm});
            skLineSegment(sketch, "E57", {"start": v(749.3, -38.1) * mm, "end": v(749.3, -88.9) * mm});
            skLineSegment(sketch, "E58", {"start": v(749.3, -88.9) * mm, "end": v(700.92, -63.5) * mm});
            skLineSegment(sketch, "E59", {"start": v(700.92, -63.5) * mm, "end": v(749.3, -38.1) * mm});
            skLineSegment(sketch, "E60.0.1.0", {"start": v(749.3, -110.67) * mm, "end": v(749.3, -161.47) * mm});
            skLineSegment(sketch, "E60.0.1.1", {"start": v(700.92, -136.07) * mm, "end": v(749.3, -110.67) * mm});
            skLineSegment(sketch, "E60.0.1.2", {"start": v(749.3, -161.47) * mm, "end": v(700.92, -136.07) * mm});
            skLineSegment(sketch, "E60.0.2.0", {"start": v(749.3, -183.24) * mm, "end": v(749.3, -234.04) * mm});
            skLineSegment(sketch, "E60.0.2.1", {"start": v(700.92, -208.64) * mm, "end": v(749.3, -183.24) * mm});
            skLineSegment(sketch, "E60.0.2.2", {"start": v(749.3, -234.04) * mm, "end": v(700.92, -208.64) * mm});
            skLineSegment(sketch, "E60.0.3.0", {"start": v(749.3, -255.81) * mm, "end": v(749.3, -306.61) * mm});
            skLineSegment(sketch, "E60.0.3.1", {"start": v(700.92, -281.21) * mm, "end": v(749.3, -255.81) * mm});
            skLineSegment(sketch, "E60.0.3.2", {"start": v(749.3, -306.61) * mm, "end": v(700.92, -281.21) * mm});
            skLineSegment(sketch, "E60.0.4.0", {"start": v(749.3, -328.39) * mm, "end": v(749.3, -379.19) * mm});
            skLineSegment(sketch, "E60.0.4.1", {"start": v(700.92, -353.79) * mm, "end": v(749.3, -328.39) * mm});
            skLineSegment(sketch, "E60.0.4.2", {"start": v(749.3, -379.19) * mm, "end": v(700.92, -353.79) * mm});
            skLineSegment(sketch, "E60.0.5.0", {"start": v(749.3, -400.96) * mm, "end": v(749.3, -451.76) * mm});
            skLineSegment(sketch, "E60.0.5.1", {"start": v(700.92, -426.36) * mm, "end": v(749.3, -400.96) * mm});
            skLineSegment(sketch, "E60.0.5.2", {"start": v(749.3, -451.76) * mm, "end": v(700.92, -426.36) * mm});
            skLineSegment(sketch, "E60.0.6.0", {"start": v(749.3, -473.53) * mm, "end": v(749.3, -524.33) * mm});
            skLineSegment(sketch, "E60.0.6.1", {"start": v(700.92, -498.93) * mm, "end": v(749.3, -473.53) * mm});
            skLineSegment(sketch, "E60.0.6.2", {"start": v(749.3, -524.33) * mm, "end": v(700.92, -498.93) * mm});
            skLineSegment(sketch, "E60.0.7.0", {"start": v(749.3, -546.1) * mm, "end": v(749.3, -596.9) * mm});
            skLineSegment(sketch, "E60.0.7.1", {"start": v(700.92, -571.5) * mm, "end": v(749.3, -546.1) * mm});
            skLineSegment(sketch, "E60.0.7.2", {"start": v(749.3, -596.9) * mm, "end": v(700.92, -571.5) * mm});
            skLineSegment(sketch, "E60.direction1", {"start": v(749.3, -88.9) * mm, "end": v(774.7, -88.9) * mm, "construction": true});
            skLineSegment(sketch, "E60.direction2", {"start": v(749.3, -88.9) * mm, "end": v(749.3, -161.47) * mm, "construction": true});
            skLineSegment(sketch, "E61.0.1.0", {"start": v(48.99, -174.17) * mm, "end": v(97.37, -148.77) * mm});
            skLineSegment(sketch, "E61.0.1.1", {"start": v(145.75, -174.17) * mm, "end": v(97.37, -148.77) * mm});
            skLineSegment(sketch, "E61.0.1.2", {"start": v(97.37, -199.57) * mm, "end": v(145.75, -174.17) * mm});
            skLineSegment(sketch, "E61.0.1.3", {"start": v(97.37, -199.57) * mm, "end": v(48.99, -174.17) * mm});
            skLineSegment(sketch, "E61.0.2.0", {"start": v(48.99, -246.74) * mm, "end": v(97.37, -221.34) * mm});
            skLineSegment(sketch, "E61.0.2.1", {"start": v(145.75, -246.74) * mm, "end": v(97.37, -221.34) * mm});
            skLineSegment(sketch, "E61.0.2.2", {"start": v(97.37, -272.14) * mm, "end": v(145.75, -246.74) * mm});
            skLineSegment(sketch, "E61.0.2.3", {"start": v(97.37, -272.14) * mm, "end": v(48.99, -246.74) * mm});
            skLineSegment(sketch, "E61.0.3.0", {"start": v(48.99, -319.31) * mm, "end": v(97.37, -293.91) * mm});
            skLineSegment(sketch, "E61.0.3.1", {"start": v(145.75, -319.31) * mm, "end": v(97.37, -293.91) * mm});
            skLineSegment(sketch, "E61.0.3.2", {"start": v(97.37, -344.71) * mm, "end": v(145.75, -319.31) * mm});
            skLineSegment(sketch, "E61.0.3.3", {"start": v(97.37, -344.71) * mm, "end": v(48.99, -319.31) * mm});
            skLineSegment(sketch, "E61.0.4.0", {"start": v(48.99, -391.89) * mm, "end": v(97.37, -366.49) * mm});
            skLineSegment(sketch, "E61.0.4.1", {"start": v(145.75, -391.89) * mm, "end": v(97.37, -366.49) * mm});
            skLineSegment(sketch, "E61.0.4.2", {"start": v(97.37, -417.29) * mm, "end": v(145.75, -391.89) * mm});
            skLineSegment(sketch, "E61.0.4.3", {"start": v(97.37, -417.29) * mm, "end": v(48.99, -391.89) * mm});
            skLineSegment(sketch, "E61.0.5.0", {"start": v(48.99, -464.46) * mm, "end": v(97.37, -439.06) * mm});
            skLineSegment(sketch, "E61.0.5.1", {"start": v(145.75, -464.46) * mm, "end": v(97.37, -439.06) * mm});
            skLineSegment(sketch, "E61.0.5.2", {"start": v(97.37, -489.86) * mm, "end": v(145.75, -464.46) * mm});
            skLineSegment(sketch, "E61.0.5.3", {"start": v(97.37, -489.86) * mm, "end": v(48.99, -464.46) * mm});
            skLineSegment(sketch, "E61.0.6.0", {"start": v(48.99, -537.03) * mm, "end": v(97.37, -511.63) * mm});
            skLineSegment(sketch, "E61.0.6.1", {"start": v(145.75, -537.03) * mm, "end": v(97.37, -511.63) * mm});
            skLineSegment(sketch, "E61.0.6.2", {"start": v(97.37, -562.43) * mm, "end": v(145.75, -537.03) * mm});
            skLineSegment(sketch, "E61.0.6.3", {"start": v(97.37, -562.43) * mm, "end": v(48.99, -537.03) * mm});
            skLineSegment(sketch, "E61.1.0.0", {"start": v(167.52, -101.6) * mm, "end": v(215.9, -76.2) * mm});
            skLineSegment(sketch, "E61.1.0.1", {"start": v(264.28, -101.6) * mm, "end": v(215.9, -76.2) * mm});
            skLineSegment(sketch, "E61.1.0.2", {"start": v(215.9, -127) * mm, "end": v(264.28, -101.6) * mm});
            skLineSegment(sketch, "E61.1.0.3", {"start": v(215.9, -127) * mm, "end": v(167.52, -101.6) * mm});
            skLineSegment(sketch, "E61.1.1.0", {"start": v(167.52, -174.17) * mm, "end": v(215.9, -148.77) * mm});
            skLineSegment(sketch, "E61.1.1.1", {"start": v(264.28, -174.17) * mm, "end": v(215.9, -148.77) * mm});
            skLineSegment(sketch, "E61.1.1.2", {"start": v(215.9, -199.57) * mm, "end": v(264.28, -174.17) * mm});
            skLineSegment(sketch, "E61.1.1.3", {"start": v(215.9, -199.57) * mm, "end": v(167.52, -174.17) * mm});
            skLineSegment(sketch, "E61.1.2.0", {"start": v(167.52, -246.74) * mm, "end": v(215.9, -221.34) * mm});
            skLineSegment(sketch, "E61.1.2.1", {"start": v(264.28, -246.74) * mm, "end": v(215.9, -221.34) * mm});
            skLineSegment(sketch, "E61.1.2.2", {"start": v(215.9, -272.14) * mm, "end": v(264.28, -246.74) * mm});
            skLineSegment(sketch, "E61.1.2.3", {"start": v(215.9, -272.14) * mm, "end": v(167.52, -246.74) * mm});
            skLineSegment(sketch, "E61.1.3.0", {"start": v(167.52, -319.31) * mm, "end": v(215.9, -293.91) * mm});
            skLineSegment(sketch, "E61.1.3.1", {"start": v(264.28, -319.31) * mm, "end": v(215.9, -293.91) * mm});
            skLineSegment(sketch, "E61.1.3.2", {"start": v(215.9, -344.71) * mm, "end": v(264.28, -319.31) * mm});
            skLineSegment(sketch, "E61.1.3.3", {"start": v(215.9, -344.71) * mm, "end": v(167.52, -319.31) * mm});
            skLineSegment(sketch, "E61.1.4.0", {"start": v(167.52, -391.89) * mm, "end": v(215.9, -366.49) * mm});
            skLineSegment(sketch, "E61.1.4.1", {"start": v(264.28, -391.89) * mm, "end": v(215.9, -366.49) * mm});
            skLineSegment(sketch, "E61.1.4.2", {"start": v(215.9, -417.29) * mm, "end": v(264.28, -391.89) * mm});
            skLineSegment(sketch, "E61.1.4.3", {"start": v(215.9, -417.29) * mm, "end": v(167.52, -391.89) * mm});
            skLineSegment(sketch, "E61.1.5.0", {"start": v(167.52, -464.46) * mm, "end": v(215.9, -439.06) * mm});
            skLineSegment(sketch, "E61.1.5.1", {"start": v(264.28, -464.46) * mm, "end": v(215.9, -439.06) * mm});
            skLineSegment(sketch, "E61.1.5.2", {"start": v(215.9, -489.86) * mm, "end": v(264.28, -464.46) * mm});
            skLineSegment(sketch, "E61.1.5.3", {"start": v(215.9, -489.86) * mm, "end": v(167.52, -464.46) * mm});
            skLineSegment(sketch, "E61.1.6.0", {"start": v(167.52, -537.03) * mm, "end": v(215.9, -511.63) * mm});
            skLineSegment(sketch, "E61.1.6.1", {"start": v(264.28, -537.03) * mm, "end": v(215.9, -511.63) * mm});
            skLineSegment(sketch, "E61.1.6.2", {"start": v(215.9, -562.43) * mm, "end": v(264.28, -537.03) * mm});
            skLineSegment(sketch, "E61.1.6.3", {"start": v(215.9, -562.43) * mm, "end": v(167.52, -537.03) * mm});
            skLineSegment(sketch, "E61.2.0.0", {"start": v(286.05, -101.6) * mm, "end": v(334.43, -76.2) * mm});
            skLineSegment(sketch, "E61.2.0.1", {"start": v(382.81, -101.6) * mm, "end": v(334.43, -76.2) * mm});
            skLineSegment(sketch, "E61.2.0.2", {"start": v(334.43, -127) * mm, "end": v(382.81, -101.6) * mm});
            skLineSegment(sketch, "E61.2.0.3", {"start": v(334.43, -127) * mm, "end": v(286.05, -101.6) * mm});
            skLineSegment(sketch, "E61.2.1.0", {"start": v(286.05, -174.17) * mm, "end": v(334.43, -148.77) * mm});
            skLineSegment(sketch, "E61.2.1.1", {"start": v(382.81, -174.17) * mm, "end": v(334.43, -148.77) * mm});
            skLineSegment(sketch, "E61.2.1.2", {"start": v(334.43, -199.57) * mm, "end": v(382.81, -174.17) * mm});
            skLineSegment(sketch, "E61.2.1.3", {"start": v(334.43, -199.57) * mm, "end": v(286.05, -174.17) * mm});
            skLineSegment(sketch, "E61.2.2.0", {"start": v(286.05, -246.74) * mm, "end": v(334.43, -221.34) * mm});
            skLineSegment(sketch, "E61.2.2.1", {"start": v(382.81, -246.74) * mm, "end": v(334.43, -221.34) * mm});
            skLineSegment(sketch, "E61.2.2.2", {"start": v(334.43, -272.14) * mm, "end": v(382.81, -246.74) * mm});
            skLineSegment(sketch, "E61.2.2.3", {"start": v(334.43, -272.14) * mm, "end": v(286.05, -246.74) * mm});
            skLineSegment(sketch, "E61.2.3.0", {"start": v(286.05, -319.31) * mm, "end": v(334.43, -293.91) * mm});
            skLineSegment(sketch, "E61.2.3.1", {"start": v(382.81, -319.31) * mm, "end": v(334.43, -293.91) * mm});
            skLineSegment(sketch, "E61.2.3.2", {"start": v(334.43, -344.71) * mm, "end": v(382.81, -319.31) * mm});
            skLineSegment(sketch, "E61.2.3.3", {"start": v(334.43, -344.71) * mm, "end": v(286.05, -319.31) * mm});
            skLineSegment(sketch, "E61.2.4.0", {"start": v(286.05, -391.89) * mm, "end": v(334.43, -366.49) * mm});
            skLineSegment(sketch, "E61.2.4.1", {"start": v(382.81, -391.89) * mm, "end": v(334.43, -366.49) * mm});
            skLineSegment(sketch, "E61.2.4.2", {"start": v(334.43, -417.29) * mm, "end": v(382.81, -391.89) * mm});
            skLineSegment(sketch, "E61.2.4.3", {"start": v(334.43, -417.29) * mm, "end": v(286.05, -391.89) * mm});
            skLineSegment(sketch, "E61.2.5.0", {"start": v(286.05, -464.46) * mm, "end": v(334.43, -439.06) * mm});
            skLineSegment(sketch, "E61.2.5.1", {"start": v(382.81, -464.46) * mm, "end": v(334.43, -439.06) * mm});
            skLineSegment(sketch, "E61.2.5.2", {"start": v(334.43, -489.86) * mm, "end": v(382.81, -464.46) * mm});
            skLineSegment(sketch, "E61.2.5.3", {"start": v(334.43, -489.86) * mm, "end": v(286.05, -464.46) * mm});
            skLineSegment(sketch, "E61.2.6.0", {"start": v(286.05, -537.03) * mm, "end": v(334.43, -511.63) * mm});
            skLineSegment(sketch, "E61.2.6.1", {"start": v(382.81, -537.03) * mm, "end": v(334.43, -511.63) * mm});
            skLineSegment(sketch, "E61.2.6.2", {"start": v(334.43, -562.43) * mm, "end": v(382.81, -537.03) * mm});
            skLineSegment(sketch, "E61.2.6.3", {"start": v(334.43, -562.43) * mm, "end": v(286.05, -537.03) * mm});
            skLineSegment(sketch, "E61.3.0.0", {"start": v(404.59, -101.6) * mm, "end": v(452.97, -76.2) * mm, "construction": true});
            skLineSegment(sketch, "E61.3.0.3", {"start": v(452.97, -127) * mm, "end": v(404.59, -101.6) * mm, "construction": true});
            skLineSegment(sketch, "E61.3.1.0", {"start": v(404.59, -174.17) * mm, "end": v(452.97, -148.77) * mm});
            skLineSegment(sketch, "E61.3.1.1", {"start": v(501.35, -174.17) * mm, "end": v(452.97, -148.77) * mm});
            skLineSegment(sketch, "E61.3.1.2", {"start": v(452.97, -199.57) * mm, "end": v(501.35, -174.17) * mm});
            skLineSegment(sketch, "E61.3.1.3", {"start": v(452.97, -199.57) * mm, "end": v(404.59, -174.17) * mm});
            skLineSegment(sketch, "E61.3.2.0", {"start": v(404.59, -246.74) * mm, "end": v(452.97, -221.34) * mm});
            skLineSegment(sketch, "E61.3.2.1", {"start": v(501.35, -246.74) * mm, "end": v(452.97, -221.34) * mm});
            skLineSegment(sketch, "E61.3.2.2", {"start": v(452.97, -272.14) * mm, "end": v(501.35, -246.74) * mm});
            skLineSegment(sketch, "E61.3.2.3", {"start": v(452.97, -272.14) * mm, "end": v(404.59, -246.74) * mm});
            skLineSegment(sketch, "E61.3.3.0", {"start": v(404.59, -319.31) * mm, "end": v(452.97, -293.91) * mm});
            skLineSegment(sketch, "E61.3.3.1", {"start": v(501.35, -319.31) * mm, "end": v(452.97, -293.91) * mm});
            skLineSegment(sketch, "E61.3.3.2", {"start": v(452.97, -344.71) * mm, "end": v(501.35, -319.31) * mm});
            skLineSegment(sketch, "E61.3.3.3", {"start": v(452.97, -344.71) * mm, "end": v(404.59, -319.31) * mm});
            skLineSegment(sketch, "E61.3.4.0", {"start": v(404.59, -391.89) * mm, "end": v(452.97, -366.49) * mm});
            skLineSegment(sketch, "E61.3.4.1", {"start": v(501.35, -391.89) * mm, "end": v(452.97, -366.49) * mm});
            skLineSegment(sketch, "E61.3.4.2", {"start": v(452.97, -417.29) * mm, "end": v(501.35, -391.89) * mm});
            skLineSegment(sketch, "E61.3.4.3", {"start": v(452.97, -417.29) * mm, "end": v(404.59, -391.89) * mm});
            skLineSegment(sketch, "E61.3.5.0", {"start": v(404.59, -464.46) * mm, "end": v(452.97, -439.06) * mm});
            skLineSegment(sketch, "E61.3.5.1", {"start": v(501.35, -464.46) * mm, "end": v(452.97, -439.06) * mm});
            skLineSegment(sketch, "E61.3.5.2", {"start": v(452.97, -489.86) * mm, "end": v(501.35, -464.46) * mm});
            skLineSegment(sketch, "E61.3.5.3", {"start": v(452.97, -489.86) * mm, "end": v(404.59, -464.46) * mm});
            skLineSegment(sketch, "E61.3.6.0", {"start": v(404.59, -537.03) * mm, "end": v(452.97, -511.63) * mm});
            skLineSegment(sketch, "E61.3.6.1", {"start": v(501.35, -537.03) * mm, "end": v(452.97, -511.63) * mm});
            skLineSegment(sketch, "E61.3.6.2", {"start": v(452.97, -562.43) * mm, "end": v(501.35, -537.03) * mm});
            skLineSegment(sketch, "E61.3.6.3", {"start": v(452.97, -562.43) * mm, "end": v(404.59, -537.03) * mm});
            skLineSegment(sketch, "E61.4.0.0", {"start": v(523.12, -101.6) * mm, "end": v(571.5, -76.2) * mm});
            skLineSegment(sketch, "E61.4.0.1", {"start": v(619.88, -101.6) * mm, "end": v(571.5, -76.2) * mm});
            skLineSegment(sketch, "E61.4.0.2", {"start": v(571.5, -127) * mm, "end": v(619.88, -101.6) * mm});
            skLineSegment(sketch, "E61.4.0.3", {"start": v(571.5, -127) * mm, "end": v(523.12, -101.6) * mm});
            skLineSegment(sketch, "E61.4.1.0", {"start": v(523.12, -174.17) * mm, "end": v(571.5, -148.77) * mm});
            skLineSegment(sketch, "E61.4.1.1", {"start": v(619.88, -174.17) * mm, "end": v(571.5, -148.77) * mm});
            skLineSegment(sketch, "E61.4.1.2", {"start": v(571.5, -199.57) * mm, "end": v(619.88, -174.17) * mm});
            skLineSegment(sketch, "E61.4.1.3", {"start": v(571.5, -199.57) * mm, "end": v(523.12, -174.17) * mm});
            skLineSegment(sketch, "E61.4.2.0", {"start": v(523.12, -246.74) * mm, "end": v(571.5, -221.34) * mm});
            skLineSegment(sketch, "E61.4.2.1", {"start": v(619.88, -246.74) * mm, "end": v(571.5, -221.34) * mm});
            skLineSegment(sketch, "E61.4.2.2", {"start": v(571.5, -272.14) * mm, "end": v(619.88, -246.74) * mm});
            skLineSegment(sketch, "E61.4.2.3", {"start": v(571.5, -272.14) * mm, "end": v(523.12, -246.74) * mm});
            skLineSegment(sketch, "E61.4.3.0", {"start": v(523.12, -319.31) * mm, "end": v(571.5, -293.91) * mm});
            skLineSegment(sketch, "E61.4.3.1", {"start": v(619.88, -319.31) * mm, "end": v(571.5, -293.91) * mm});
            skLineSegment(sketch, "E61.4.3.2", {"start": v(571.5, -344.71) * mm, "end": v(619.88, -319.31) * mm});
            skLineSegment(sketch, "E61.4.3.3", {"start": v(571.5, -344.71) * mm, "end": v(523.12, -319.31) * mm});
            skLineSegment(sketch, "E61.4.4.0", {"start": v(523.12, -391.89) * mm, "end": v(571.5, -366.49) * mm});
            skLineSegment(sketch, "E61.4.4.1", {"start": v(619.88, -391.89) * mm, "end": v(571.5, -366.49) * mm});
            skLineSegment(sketch, "E61.4.4.2", {"start": v(571.5, -417.29) * mm, "end": v(619.88, -391.89) * mm});
            skLineSegment(sketch, "E61.4.4.3", {"start": v(571.5, -417.29) * mm, "end": v(523.12, -391.89) * mm});
            skLineSegment(sketch, "E61.4.5.0", {"start": v(523.12, -464.46) * mm, "end": v(571.5, -439.06) * mm});
            skLineSegment(sketch, "E61.4.5.1", {"start": v(619.88, -464.46) * mm, "end": v(571.5, -439.06) * mm});
            skLineSegment(sketch, "E61.4.5.2", {"start": v(571.5, -489.86) * mm, "end": v(619.88, -464.46) * mm});
            skLineSegment(sketch, "E61.4.5.3", {"start": v(571.5, -489.86) * mm, "end": v(523.12, -464.46) * mm});
            skLineSegment(sketch, "E61.4.6.0", {"start": v(523.12, -537.03) * mm, "end": v(571.5, -511.63) * mm});
            skLineSegment(sketch, "E61.4.6.1", {"start": v(619.88, -537.03) * mm, "end": v(571.5, -511.63) * mm});
            skLineSegment(sketch, "E61.4.6.2", {"start": v(571.5, -562.43) * mm, "end": v(619.88, -537.03) * mm});
            skLineSegment(sketch, "E61.4.6.3", {"start": v(571.5, -562.43) * mm, "end": v(523.12, -537.03) * mm});
            skLineSegment(sketch, "E61.5.0.0", {"start": v(641.65, -101.6) * mm, "end": v(690.03, -76.2) * mm});
            skLineSegment(sketch, "E61.5.0.1", {"start": v(738.41, -101.6) * mm, "end": v(690.03, -76.2) * mm});
            skLineSegment(sketch, "E61.5.0.2", {"start": v(690.03, -127) * mm, "end": v(738.41, -101.6) * mm});
            skLineSegment(sketch, "E61.5.0.3", {"start": v(690.03, -127) * mm, "end": v(641.65, -101.6) * mm});
            skLineSegment(sketch, "E61.5.1.0", {"start": v(641.65, -174.17) * mm, "end": v(690.03, -148.77) * mm});
            skLineSegment(sketch, "E61.5.1.1", {"start": v(738.41, -174.17) * mm, "end": v(690.03, -148.77) * mm});
            skLineSegment(sketch, "E61.5.1.2", {"start": v(690.03, -199.57) * mm, "end": v(738.41, -174.17) * mm});
            skLineSegment(sketch, "E61.5.1.3", {"start": v(690.03, -199.57) * mm, "end": v(641.65, -174.17) * mm});
            skLineSegment(sketch, "E61.5.2.0", {"start": v(641.65, -246.74) * mm, "end": v(690.03, -221.34) * mm});
            skLineSegment(sketch, "E61.5.2.1", {"start": v(738.41, -246.74) * mm, "end": v(690.03, -221.34) * mm});
            skLineSegment(sketch, "E61.5.2.2", {"start": v(690.03, -272.14) * mm, "end": v(738.41, -246.74) * mm});
            skLineSegment(sketch, "E61.5.2.3", {"start": v(690.03, -272.14) * mm, "end": v(641.65, -246.74) * mm});
            skLineSegment(sketch, "E61.5.3.0", {"start": v(641.65, -319.31) * mm, "end": v(690.03, -293.91) * mm});
            skLineSegment(sketch, "E61.5.3.1", {"start": v(738.41, -319.31) * mm, "end": v(690.03, -293.91) * mm});
            skLineSegment(sketch, "E61.5.3.2", {"start": v(690.03, -344.71) * mm, "end": v(738.41, -319.31) * mm});
            skLineSegment(sketch, "E61.5.3.3", {"start": v(690.03, -344.71) * mm, "end": v(641.65, -319.31) * mm});
            skLineSegment(sketch, "E61.5.4.0", {"start": v(641.65, -391.89) * mm, "end": v(690.03, -366.49) * mm});
            skLineSegment(sketch, "E61.5.4.1", {"start": v(738.41, -391.89) * mm, "end": v(690.03, -366.49) * mm});
            skLineSegment(sketch, "E61.5.4.2", {"start": v(690.03, -417.29) * mm, "end": v(738.41, -391.89) * mm});
            skLineSegment(sketch, "E61.5.4.3", {"start": v(690.03, -417.29) * mm, "end": v(641.65, -391.89) * mm});
            skLineSegment(sketch, "E61.5.5.0", {"start": v(641.65, -464.46) * mm, "end": v(690.03, -439.06) * mm});
            skLineSegment(sketch, "E61.5.5.1", {"start": v(738.41, -464.46) * mm, "end": v(690.03, -439.06) * mm});
            skLineSegment(sketch, "E61.5.5.2", {"start": v(690.03, -489.86) * mm, "end": v(738.41, -464.46) * mm});
            skLineSegment(sketch, "E61.5.5.3", {"start": v(690.03, -489.86) * mm, "end": v(641.65, -464.46) * mm});
            skLineSegment(sketch, "E61.5.6.0", {"start": v(641.65, -537.03) * mm, "end": v(690.03, -511.63) * mm});
            skLineSegment(sketch, "E61.5.6.1", {"start": v(738.41, -537.03) * mm, "end": v(690.03, -511.63) * mm});
            skLineSegment(sketch, "E61.5.6.2", {"start": v(690.03, -562.43) * mm, "end": v(738.41, -537.03) * mm});
            skLineSegment(sketch, "E61.5.6.3", {"start": v(690.03, -562.43) * mm, "end": v(641.65, -537.03) * mm});
            skLineSegment(sketch, "E61.direction1", {"start": v(48.99, -101.6) * mm, "end": v(167.52, -101.6) * mm, "construction": true});
            skLineSegment(sketch, "E61.direction2", {"start": v(48.99, -101.6) * mm, "end": v(48.99, -174.17) * mm, "construction": true});
            skLineSegment(sketch, "E62.bottom", {"start": v(330.2, -25.4) * mm, "end": v(457.2, -25.4) * mm});
            skLineSegment(sketch, "E62.top", {"start": v(330.2, -158.75) * mm, "end": v(457.2, -158.75) * mm});
            skLineSegment(sketch, "E62.left", {"start": v(330.2, -25.4) * mm, "end": v(330.2, -158.75) * mm});
            skLineSegment(sketch, "E62.right", {"start": v(457.2, -25.4) * mm, "end": v(457.2, -158.75) * mm});
            skLineSegment(sketch, "E63", {"start": v(501.35, -101.6) * mm, "end": v(457.2, -78.42) * mm});
            skLineSegment(sketch, "E64", {"start": v(457.2, -124.78) * mm, "end": v(501.35, -101.6) * mm});
            skLineSegment(sketch, "E65", {"start": v(606.58, -50.8) * mm, "end": v(654.96, -50.8) * mm});
            skLineSegment(sketch, "E66", {"start": v(132.44, -50.8) * mm, "end": v(180.82, -50.8) * mm});
            skLineSegment(sketch, "E67", {"start": v(132.44, -584.2) * mm, "end": v(180.82, -584.2) * mm});
            skLineSegment(sketch, "E68", {"start": v(606.58, -584.2) * mm, "end": v(654.96, -584.2) * mm});
            skLineSegment(sketch, "E69", {"start": v(0, -190.5) * mm, "end": v(114.3, -190.5) * mm});
            skLineSegment(sketch, "E70", {"start": v(114.3, -190.5) * mm, "end": v(114.3, -444.5) * mm});
            skLineSegment(sketch, "E71", {"start": v(114.3, -444.5) * mm, "end": v(0, -444.5) * mm});
            skLineSegment(sketch, "E72.bottom", {"start": v(330.2, -609.6) * mm, "end": v(457.2, -609.6) * mm});
            skLineSegment(sketch, "E72.top", {"start": v(330.2, -476.25) * mm, "end": v(457.2, -476.25) * mm});
            skLineSegment(sketch, "E72.left", {"start": v(330.2, -609.6) * mm, "end": v(330.2, -476.25) * mm});
            skLineSegment(sketch, "E72.right", {"start": v(457.2, -609.6) * mm, "end": v(457.2, -476.25) * mm});
            skSolve(sketch);
        }
        {
            var Q0;
            {var subQ0=sQuery(id+"F0.wireOp",EDGE,"97HcrBSp-ObFl-6jX2-vVKY-8WPd2NgNERHy.left");Q0=makeQuery(id+"F0.imprint","IMPRINT",FACE,{"disambiguationData":[TD([[makeQuery(id+"F0.imprint","IMPRINT",EDGE,{"derivedFrom":subQ0}),-1.0]])]});}
            var Q1;
            {var subQ0=sQuery(id+"F0.wireOp",EDGE,"toZKPNN4-sIfS-BR0S-KHO8-RDbohETaxiId.left");Q1=makeQuery(id+"F0.imprint","IMPRINT",FACE,{"disambiguationData":[TD([[makeQuery(id+"F0.imprint","IMPRINT",EDGE,{"derivedFrom":subQ0}),1.0]])]});}
            var Q2;
            {var subQ0=sQuery(id+"F0.wireOp",EDGE,"97HcrBSp-ObFl-6jX2-vVKY-8WPd2NgNERHy.right");Q2=makeQuery(id+"F0.imprint","IMPRINT",FACE,{"disambiguationData":[TD([[makeQuery(id+"F0.imprint","IMPRINT",EDGE,{"derivedFrom":subQ0}),1.0]])]});}
            var Q3;
            {var subQ0=sQuery(id+"F0.wireOp",EDGE,"toZKPNN4-sIfS-BR0S-KHO8-RDbohETaxiId.right");Q3=makeQuery(id+"F0.imprint","IMPRINT",FACE,{"disambiguationData":[TD([[makeQuery(id+"F0.imprint","IMPRINT",EDGE,{"derivedFrom":subQ0}),-1.0]])]});}
            var Q4;
            {var subQ0=sQuery(id+"F0.wireOp",EDGE,"xEcBvNq9-zX55-gM1o-iK8W-qltObQm34F43");Q4=makeQuery(id+"F0.imprint","IMPRINT",FACE,{"disambiguationData":[TD([[makeQuery(id+"F0.imprint","IMPRINT",EDGE,{"derivedFrom":subQ0}),-1.0]])]});}
            var Q5;
            {var subQ0=sQuery(id+"F0.wireOp",EDGE,"yWhyTgVt-jL2e-qkD6-lMDP-fowTrUB0jy7p");Q5=makeQuery(id+"F0.imprint","IMPRINT",FACE,{"disambiguationData":[TD([[makeQuery(id+"F0.imprint","IMPRINT",EDGE,{"derivedFrom":subQ0}),-1.0]])]});}
            var Q6;
            {var subQ0=sQuery(id+"F0.wireOp",EDGE,"GruNc9m8-yqkU-QK90-yJTr-XDLUWnV8KJXX");Q6=makeQuery(id+"F0.imprint","IMPRINT",FACE,{"disambiguationData":[TD([[makeQuery(id+"F0.imprint","IMPRINT",EDGE,{"derivedFrom":subQ0}),1.0]])]});}
            var Q7;
            {var subQ3=sQuery(id+"F0.wireOp",EDGE,"E30.left");var subQ5=sQuery(id+"F0.wireOp",EDGE,"E61.2.0.1");var subQ10=makeQuery(id+"F0.imprint","INTERSECT",VERTEX,{"derivedFrom":[subQ3,subQ5]});Q7=makeQuery(id+"F0.imprint","IMPRINT",FACE,{"disambiguationData":[TD([[makeQuery(id+"F0.imprint","IMPRINT",EDGE,{"disambiguationData":[TD([[subQ10,-1.0]])],"derivedFrom":subQ3}),-1.0]])]});}
            var Q8;
            {var subQ0=sQuery(id+"F0.wireOp",EDGE,"E62.bottom");var subQ1=sQuery(id+"F0.wireOp",EDGE,"E30.left");var subQ2=makeQuery(id+"F0.imprint","INTERSECT",VERTEX,{"derivedFrom":[subQ1,subQ0]});Q8=makeQuery(id+"F0.imprint","IMPRINT",FACE,{"disambiguationData":[TD([[makeQuery(id+"F0.imprint","IMPRINT",EDGE,{"disambiguationData":[TD([[subQ2,-1.0]])],"derivedFrom":subQ1}),-1.0]])]});}
            var Q9;
            {var subQ3=sQuery(id+"F0.wireOp",EDGE,"E30.left");var subQ6=sQuery(id+"F0.wireOp",EDGE,"E30.top");var subQ10=makeQuery(id+"F0.imprint","INTERSECT",VERTEX,{"derivedFrom":[subQ6,subQ3]});Q9=makeQuery(id+"F0.imprint","IMPRINT",FACE,{"disambiguationData":[TD([[makeQuery(id+"F0.imprint","IMPRINT",EDGE,{"disambiguationData":[TD([[subQ10,-1.0]])],"derivedFrom":subQ6}),-1.0]])]});}
            var Q10;
            {var subQ0=sQuery(id+"F0.wireOp",EDGE,"E61.2.1.1");var subQ1=sQuery(id+"F0.wireOp",EDGE,"E61.2.1.0");var subQ2=makeQuery(id+"F0.imprint","INTERSECT",VERTEX,{"derivedFrom":[subQ1,subQ0]});Q10=makeQuery(id+"F0.imprint","IMPRINT",FACE,{"disambiguationData":[TD([[makeQuery(id+"F0.imprint","IMPRINT",EDGE,{"disambiguationData":[TD([[subQ2,1.0]])],"derivedFrom":subQ1}),-1.0]])]});}
            var Q11;
            {var subQ0=sQuery(id+"F0.wireOp",EDGE,"E54.2.1.3");var subQ1=sQuery(id+"F0.wireOp",EDGE,"E30.top");var subQ2=makeQuery(id+"F0.imprint","INTERSECT",VERTEX,{"derivedFrom":[subQ1,subQ0]});Q11=makeQuery(id+"F0.imprint","IMPRINT",FACE,{"disambiguationData":[TD([[makeQuery(id+"F0.imprint","IMPRINT",EDGE,{"disambiguationData":[TD([[subQ2,-1.0]])],"derivedFrom":subQ1}),-1.0]])]});}
            var Q12;
            {var subQ5=sQuery(id+"F0.wireOp",EDGE,"E30.right");Q12=makeQuery(id+"F0.imprint","IMPRINT",FACE,{"disambiguationData":[TD([[makeQuery(id+"F0.imprint","IMPRINT",EDGE,{"derivedFrom":subQ5}),1.0]])]});}
            var Q13;
            {var subQ0=sQuery(id+"F0.wireOp",EDGE,"E61.3.1.1");var subQ1=sQuery(id+"F0.wireOp",EDGE,"E61.3.1.0");var subQ2=makeQuery(id+"F0.imprint","INTERSECT",VERTEX,{"derivedFrom":[subQ1,subQ0]});Q13=makeQuery(id+"F0.imprint","IMPRINT",FACE,{"disambiguationData":[TD([[makeQuery(id+"F0.imprint","IMPRINT",EDGE,{"disambiguationData":[TD([[subQ2,1.0]])],"derivedFrom":subQ1}),-1.0]])]});}
            var Q14;
            {var subQ3=sQuery(id+"F0.wireOp",EDGE,"E68");Q14=makeQuery(id+"F0.imprint","IMPRINT",FACE,{"disambiguationData":[TD([[makeQuery(id+"F0.imprint","IMPRINT",EDGE,{"derivedFrom":subQ3}),-1.0]])]});}
            var Q15;
            {var subQ3=sQuery(id+"F0.wireOp",EDGE,"E67");Q15=makeQuery(id+"F0.imprint","IMPRINT",FACE,{"disambiguationData":[TD([[makeQuery(id+"F0.imprint","IMPRINT",EDGE,{"derivedFrom":subQ3}),-1.0]])]});}
            var Q16;
            {var subQ1=sQuery(id+"F0.wireOp",EDGE,"E49");var subQ3=sQuery(id+"F0.wireOp",EDGE,"E66");var subQ4=makeQuery(id+"F0.imprint","INTERSECT",VERTEX,{"derivedFrom":[subQ1,subQ3]});Q16=makeQuery(id+"F0.imprint","IMPRINT",FACE,{"disambiguationData":[TD([[makeQuery(id+"F0.imprint","IMPRINT",EDGE,{"disambiguationData":[TD([[subQ4,-1.0]])],"derivedFrom":subQ3}),1.0]])]});}
            var Q17;
            Q17=makeQuery(id+"F0.imprint","IMPRINT",FACE,{"disambiguationData":[TD([[makeQuery(id+"F0.imprint","IMPRINT",EDGE,{"derivedFrom":sQuery(id+"F0.wireOp",EDGE,"E1")}),-1.0]])]});
            var Q18;
            {var subQ1=sQuery(id+"F0.wireOp",EDGE,"E50");var subQ3=sQuery(id+"F0.wireOp",EDGE,"E66");var subQ4=makeQuery(id+"F0.imprint","INTERSECT",VERTEX,{"derivedFrom":[subQ1,subQ3]});Q18=makeQuery(id+"F0.imprint","IMPRINT",FACE,{"disambiguationData":[TD([[makeQuery(id+"F0.imprint","IMPRINT",EDGE,{"disambiguationData":[TD([[subQ4,1.0]])],"derivedFrom":subQ3}),1.0]])]});}
            var Q19;
            {var subQ3=sQuery(id+"F0.wireOp",EDGE,"E65");Q19=makeQuery(id+"F0.imprint","IMPRINT",FACE,{"disambiguationData":[TD([[makeQuery(id+"F0.imprint","IMPRINT",EDGE,{"derivedFrom":subQ3}),1.0]])]});}
            var Q20;
            {var subQ19=sQuery(id+"F0.wireOp",EDGE,"E31.bottom");Q20=makeQuery(id+"F0.imprint","IMPRINT",FACE,{"disambiguationData":[TD([[makeQuery(id+"F0.imprint","IMPRINT",EDGE,{"derivedFrom":subQ19}),1.0]])]});}
            var Q21;
            {var subQ0=sQuery(id+"F0.wireOp",EDGE,"E61.0.1.3");var subQ1=sQuery(id+"F0.wireOp",EDGE,"E61.0.1.2");var subQ2=makeQuery(id+"F0.imprint","INTERSECT",VERTEX,{"derivedFrom":[subQ1,subQ0]});Q21=makeQuery(id+"F0.imprint","IMPRINT",FACE,{"disambiguationData":[TD([[makeQuery(id+"F0.imprint","IMPRINT",EDGE,{"disambiguationData":[TD([[subQ2,-1.0]])],"derivedFrom":subQ1}),1.0]])]});}
            var Q22;
            {var subQ0=sQuery(id+"F0.wireOp",EDGE,"E61.0.2.1");var subQ1=sQuery(id+"F0.wireOp",EDGE,"E31.right");var subQ2=makeQuery(id+"F0.imprint","INTERSECT",VERTEX,{"derivedFrom":[subQ1,subQ0]});Q22=makeQuery(id+"F0.imprint","IMPRINT",FACE,{"disambiguationData":[TD([[makeQuery(id+"F0.imprint","IMPRINT",EDGE,{"disambiguationData":[TD([[subQ2,-1.0]])],"derivedFrom":subQ1}),1.0]])]});}
            var Q23;
            {var subQ0=sQuery(id+"F0.wireOp",EDGE,"E56.9.0.2");var subQ1=sQuery(id+"F0.wireOp",EDGE,"E56.0.0.2");var subQ2=makeQuery(id+"F0.imprint","INTERSECT",VERTEX,{"derivedFrom":[subQ1,subQ0]});Q23=makeQuery(id+"F0.imprint","IMPRINT",FACE,{"disambiguationData":[TD([[makeQuery(id+"F0.imprint","IMPRINT",EDGE,{"disambiguationData":[TD([[subQ2,-1.0]])],"derivedFrom":subQ1}),-1.0]])]});}
            var Q24;
            {var subQ0=sQuery(id+"F0.wireOp",EDGE,"E61.0.2.2");var subQ1=sQuery(id+"F0.wireOp",EDGE,"E31.right");var subQ2=makeQuery(id+"F0.imprint","INTERSECT",VERTEX,{"derivedFrom":[subQ1,subQ0]});Q24=makeQuery(id+"F0.imprint","IMPRINT",FACE,{"disambiguationData":[TD([[makeQuery(id+"F0.imprint","IMPRINT",EDGE,{"disambiguationData":[TD([[subQ2,-1.0]])],"derivedFrom":subQ1}),1.0]])]});}
            var Q25;
            {var subQ0=sQuery(id+"F0.wireOp",EDGE,"E61.0.3.2");var subQ1=sQuery(id+"F0.wireOp",EDGE,"E31.right");var subQ2=makeQuery(id+"F0.imprint","INTERSECT",VERTEX,{"derivedFrom":[subQ1,subQ0]});Q25=makeQuery(id+"F0.imprint","IMPRINT",FACE,{"disambiguationData":[TD([[makeQuery(id+"F0.imprint","IMPRINT",EDGE,{"disambiguationData":[TD([[subQ2,-1.0]])],"derivedFrom":subQ1}),1.0]])]});}
            var Q26;
            {var subQ0=sQuery(id+"F0.wireOp",EDGE,"E56.9.0.4");var subQ1=sQuery(id+"F0.wireOp",EDGE,"E56.0.0.4");var subQ2=makeQuery(id+"F0.imprint","INTERSECT",VERTEX,{"derivedFrom":[subQ1,subQ0]});Q26=makeQuery(id+"F0.imprint","IMPRINT",FACE,{"disambiguationData":[TD([[makeQuery(id+"F0.imprint","IMPRINT",EDGE,{"disambiguationData":[TD([[subQ2,-1.0]])],"derivedFrom":subQ1}),-1.0]])]});}
            var Q27;
            {var subQ0=sQuery(id+"F0.wireOp",EDGE,"E56.9.0.3");var subQ1=sQuery(id+"F0.wireOp",EDGE,"E56.0.0.3");var subQ2=makeQuery(id+"F0.imprint","INTERSECT",VERTEX,{"derivedFrom":[subQ1,subQ0]});Q27=makeQuery(id+"F0.imprint","IMPRINT",FACE,{"disambiguationData":[TD([[makeQuery(id+"F0.imprint","IMPRINT",EDGE,{"disambiguationData":[TD([[subQ2,-1.0]])],"derivedFrom":subQ1}),-1.0]])]});}
            var Q28;
            {var subQ0=sQuery(id+"F0.wireOp",EDGE,"E61.0.3.1");var subQ1=sQuery(id+"F0.wireOp",EDGE,"E31.right");var subQ2=makeQuery(id+"F0.imprint","INTERSECT",VERTEX,{"derivedFrom":[subQ1,subQ0]});Q28=makeQuery(id+"F0.imprint","IMPRINT",FACE,{"disambiguationData":[TD([[makeQuery(id+"F0.imprint","IMPRINT",EDGE,{"disambiguationData":[TD([[subQ2,-1.0]])],"derivedFrom":subQ1}),1.0]])]});}
            var Q29;
            {var subQ0=sQuery(id+"F0.wireOp",EDGE,"E61.0.4.1");var subQ1=sQuery(id+"F0.wireOp",EDGE,"E31.right");var subQ2=makeQuery(id+"F0.imprint","INTERSECT",VERTEX,{"derivedFrom":[subQ1,subQ0]});Q29=makeQuery(id+"F0.imprint","IMPRINT",FACE,{"disambiguationData":[TD([[makeQuery(id+"F0.imprint","IMPRINT",EDGE,{"disambiguationData":[TD([[subQ2,-1.0]])],"derivedFrom":subQ1}),1.0]])]});}
            var Q30;
            {var subQ0=sQuery(id+"F0.wireOp",EDGE,"E61.0.5.1");var subQ1=sQuery(id+"F0.wireOp",EDGE,"E61.0.5.0");var subQ2=makeQuery(id+"F0.imprint","INTERSECT",VERTEX,{"derivedFrom":[subQ1,subQ0]});Q30=makeQuery(id+"F0.imprint","IMPRINT",FACE,{"disambiguationData":[TD([[makeQuery(id+"F0.imprint","IMPRINT",EDGE,{"disambiguationData":[TD([[subQ2,1.0]])],"derivedFrom":subQ1}),-1.0]])]});}
            var Q31;
            {var subQ0=sQuery(id+"F0.wireOp",EDGE,"E56.9.0.5");var subQ1=sQuery(id+"F0.wireOp",EDGE,"E56.0.0.5");var subQ2=makeQuery(id+"F0.imprint","INTERSECT",VERTEX,{"derivedFrom":[subQ1,subQ0]});Q31=makeQuery(id+"F0.imprint","IMPRINT",FACE,{"disambiguationData":[TD([[makeQuery(id+"F0.imprint","IMPRINT",EDGE,{"disambiguationData":[TD([[subQ2,-1.0]])],"derivedFrom":subQ1}),-1.0]])]});}
            var Q32;
            {var subQ18=sQuery(id+"F0.wireOp",EDGE,"E31.top");Q32=makeQuery(id+"F0.imprint","IMPRINT",FACE,{"disambiguationData":[TD([[makeQuery(id+"F0.imprint","IMPRINT",EDGE,{"derivedFrom":subQ18}),-1.0]])]});}
            var Q33;
            {var subQ0=sQuery(id+"F0.wireOp",EDGE,"E56.3.2.6");var subQ1=sQuery(id+"F0.wireOp",EDGE,"E29.top");var subQ2=makeQuery(id+"F0.imprint","INTERSECT",VERTEX,{"derivedFrom":[subQ1,subQ0]});Q33=makeQuery(id+"F0.imprint","IMPRINT",FACE,{"disambiguationData":[TD([[makeQuery(id+"F0.imprint","IMPRINT",EDGE,{"disambiguationData":[TD([[subQ2,-1.0]])],"derivedFrom":subQ1}),-1.0]])]});}
            var Q34;
            {var subQ5=sQuery(id+"F0.wireOp",EDGE,"E72.bottom");var subQ6=sQuery(id+"F0.wireOp",EDGE,"E29.right");var subQ7=makeQuery(id+"F0.imprint","INTERSECT",VERTEX,{"derivedFrom":[subQ6,subQ5]});Q34=makeQuery(id+"F0.imprint","IMPRINT",FACE,{"disambiguationData":[TD([[makeQuery(id+"F0.imprint","IMPRINT",EDGE,{"disambiguationData":[TD([[subQ7,-1.0]])],"derivedFrom":subQ6}),1.0]])]});}
            var Q35;
            {var subQ1=sQuery(id+"F0.wireOp",EDGE,"E61.2.6.2");var subQ3=sQuery(id+"F0.wireOp",EDGE,"E29.right");var subQ4=makeQuery(id+"F0.imprint","INTERSECT",VERTEX,{"derivedFrom":[subQ3,subQ1]});Q35=makeQuery(id+"F0.imprint","IMPRINT",FACE,{"disambiguationData":[TD([[makeQuery(id+"F0.imprint","IMPRINT",EDGE,{"disambiguationData":[TD([[subQ4,-1.0]])],"derivedFrom":subQ3}),1.0]])]});}
            var Q36;
            {var subQ1=sQuery(id+"F0.wireOp",EDGE,"E29.top");var subQ5=sQuery(id+"F0.wireOp",EDGE,"E29.right");var subQ6=makeQuery(id+"F0.imprint","INTERSECT",VERTEX,{"derivedFrom":[subQ1,subQ5]});Q36=makeQuery(id+"F0.imprint","IMPRINT",FACE,{"disambiguationData":[TD([[makeQuery(id+"F0.imprint","IMPRINT",EDGE,{"disambiguationData":[TD([[subQ6,1.0]])],"derivedFrom":subQ1}),-1.0]])]});}
            var Q37;
            {var subQ0=sQuery(id+"F0.wireOp",EDGE,"E61.2.5.3");var subQ1=sQuery(id+"F0.wireOp",EDGE,"E61.2.5.2");var subQ2=makeQuery(id+"F0.imprint","INTERSECT",VERTEX,{"derivedFrom":[subQ1,subQ0]});Q37=makeQuery(id+"F0.imprint","IMPRINT",FACE,{"disambiguationData":[TD([[makeQuery(id+"F0.imprint","IMPRINT",EDGE,{"disambiguationData":[TD([[subQ2,-1.0]])],"derivedFrom":subQ1}),1.0]])]});}
            var Q38;
            {var subQ0=sQuery(id+"F0.wireOp",EDGE,"E61.3.5.3");var subQ1=sQuery(id+"F0.wireOp",EDGE,"E61.3.5.2");var subQ2=makeQuery(id+"F0.imprint","INTERSECT",VERTEX,{"derivedFrom":[subQ1,subQ0]});Q38=makeQuery(id+"F0.imprint","IMPRINT",FACE,{"disambiguationData":[TD([[makeQuery(id+"F0.imprint","IMPRINT",EDGE,{"disambiguationData":[TD([[subQ2,-1.0]])],"derivedFrom":subQ1}),1.0]])]});}
            var Q39;
            {var subQ6=sQuery(id+"F0.wireOp",EDGE,"E29.top");var subQ10=sQuery(id+"F0.wireOp",EDGE,"E29.left");var subQ11=makeQuery(id+"F0.imprint","INTERSECT",VERTEX,{"derivedFrom":[subQ6,subQ10]});Q39=makeQuery(id+"F0.imprint","IMPRINT",FACE,{"disambiguationData":[TD([[makeQuery(id+"F0.imprint","IMPRINT",EDGE,{"disambiguationData":[TD([[subQ11,-1.0]])],"derivedFrom":subQ6}),-1.0]])]});}
            var Q40;
            {var subQ0=sQuery(id+"F0.wireOp",EDGE,"E61.3.6.3");var subQ9=sQuery(id+"F0.wireOp",EDGE,"E29.left");var subQ11=makeQuery(id+"F0.imprint","INTERSECT",VERTEX,{"derivedFrom":[subQ9,subQ0]});Q40=makeQuery(id+"F0.imprint","IMPRINT",FACE,{"disambiguationData":[TD([[makeQuery(id+"F0.imprint","IMPRINT",EDGE,{"disambiguationData":[TD([[subQ11,-1.0]])],"derivedFrom":subQ9}),-1.0]])]});}
            var Q41;
            {var subQ3=sQuery(id+"F0.wireOp",EDGE,"E29.left");var subQ5=sQuery(id+"F0.wireOp",EDGE,"E72.bottom");var subQ6=makeQuery(id+"F0.imprint","INTERSECT",VERTEX,{"derivedFrom":[subQ3,subQ5]});Q41=makeQuery(id+"F0.imprint","IMPRINT",FACE,{"disambiguationData":[TD([[makeQuery(id+"F0.imprint","IMPRINT",EDGE,{"disambiguationData":[TD([[subQ6,-1.0]])],"derivedFrom":subQ3}),-1.0]])]});}
            extrude(context, id + "F1", {"entities" : qUnion([Q0, Q1, Q2, Q3, Q4, Q5, Q6, Q7, Q8, Q9, Q10, Q11, Q12, Q13, Q14, Q15, Q16, Q17, Q18, Q19, Q20, Q21, Q22, Q23, Q24, Q25, Q26, Q27, Q28, Q29, Q30, Q31, Q32, Q33, Q34, Q35, Q36, Q37, Q38, Q39, Q40, Q41]), "depth" : 3.17 * mm, "offsetDistance" : 25.4 * mm});
        }
    });
